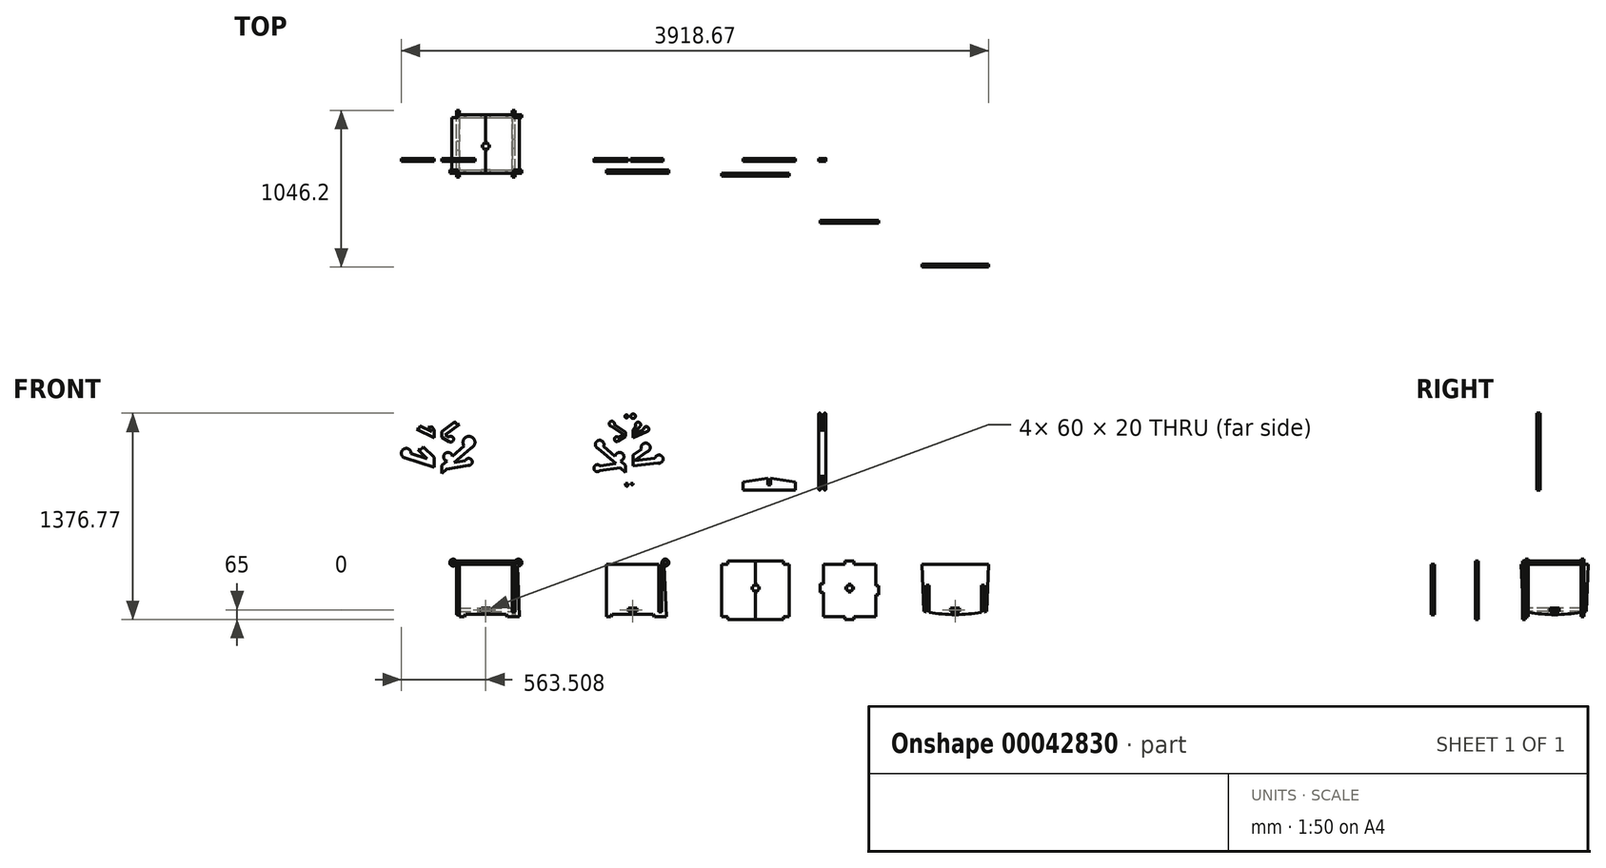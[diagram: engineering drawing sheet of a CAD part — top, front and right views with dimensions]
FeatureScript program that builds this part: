
annotation { "Feature Type Name" : "Feature", "Feature Type Description" : "" }
export const myFeature = defineFeature(function(context is Context, id is Id, definition is map)
    precondition{}
    {
        {
            var Q0;
            Q0=qCreatedBy(makeId("Top.planeOp"),FACE);
            var sketch = newSketch(context, id + "F0", { "sketchPlane" : qUnion([Q0])});
            skLineSegment(sketch, "E0.bottom", {"start": v(249.97, 292.99) * mm, "end": v(599.97, 292.99) * mm});
            skLineSegment(sketch, "E0.top", {"start": v(249.97, -57.01) * mm, "end": v(599.97, -57.01) * mm});
            skLineSegment(sketch, "E0.left", {"start": v(249.97, 292.99) * mm, "end": v(249.97, -57.01) * mm});
            skLineSegment(sketch, "E0.right", {"start": v(599.97, 292.99) * mm, "end": v(599.97, -57.01) * mm});
            skLineSegment(sketch, "E1.rect.bottom", {"start": v(454.97, -77.01) * mm, "end": v(394.97, -77.01) * mm});
            skLineSegment(sketch, "E1.rect.top", {"start": v(454.97, -37.01) * mm, "end": v(394.97, -37.01) * mm});
            skLineSegment(sketch, "E1.rect.left", {"start": v(454.97, -77.01) * mm, "end": v(454.97, -37.01) * mm});
            skLineSegment(sketch, "E1.rect.right", {"start": v(394.97, -77.01) * mm, "end": v(394.97, -37.01) * mm});
            skPoint(sketch, "E1.rect.middle", {"position": v(424.97, -57.01) * mm});
            skLineSegment(sketch, "E2.rect.bottom", {"start": v(269.97, 73.3) * mm, "end": v(229.97, 73.3) * mm});
            skLineSegment(sketch, "E2.rect.top", {"start": v(269.97, 133.3) * mm, "end": v(229.97, 133.3) * mm});
            skLineSegment(sketch, "E2.rect.left", {"start": v(269.97, 73.3) * mm, "end": v(269.97, 133.3) * mm});
            skLineSegment(sketch, "E2.rect.right", {"start": v(229.97, 73.3) * mm, "end": v(229.97, 133.3) * mm});
            skPoint(sketch, "E2.rect.middle", {"position": v(249.97, 103.3) * mm});
            skLineSegment(sketch, "E3.rect.bottom", {"start": v(454.97, 272.99) * mm, "end": v(394.97, 272.99) * mm});
            skLineSegment(sketch, "E3.rect.top", {"start": v(454.97, 312.99) * mm, "end": v(394.97, 312.99) * mm});
            skLineSegment(sketch, "E3.rect.left", {"start": v(454.97, 272.99) * mm, "end": v(454.97, 312.99) * mm});
            skLineSegment(sketch, "E3.rect.right", {"start": v(394.97, 272.99) * mm, "end": v(394.97, 312.99) * mm});
            skPoint(sketch, "E3.rect.middle", {"position": v(424.97, 292.99) * mm});
            skLineSegment(sketch, "E4.rect.bottom", {"start": v(619.97, 87.99) * mm, "end": v(579.97, 87.99) * mm});
            skLineSegment(sketch, "E4.rect.top", {"start": v(619.97, 147.99) * mm, "end": v(579.97, 147.99) * mm});
            skLineSegment(sketch, "E4.rect.left", {"start": v(619.97, 87.99) * mm, "end": v(619.97, 147.99) * mm});
            skLineSegment(sketch, "E4.rect.right", {"start": v(579.97, 87.99) * mm, "end": v(579.97, 147.99) * mm});
            skPoint(sketch, "E4.rect.middle", {"position": v(599.97, 117.99) * mm});
            skSolve(sketch);
        }
        {
            var Q0;
            Q0=makeQuery(id+"F0.imprint","IMPRINT",FACE,{"disambiguationData":[TD([[makeQuery(id+"F0.imprint","IMPRINT",EDGE,{"derivedFrom":sQuery(id+"F0.wireOp",EDGE,"E0.bottom")}),-1.0]])]});
            var Q1;
            {var subQ3=sQuery(id+"F0.wireOp",EDGE,"E2.rect.right");Q1=makeQuery(id+"F0.imprint","IMPRINT",FACE,{"disambiguationData":[TD([[makeQuery(id+"F0.imprint","IMPRINT",EDGE,{"derivedFrom":subQ3}),-1.0]])]});}
            var Q2;
            {var subQ3=sQuery(id+"F0.wireOp",EDGE,"E3.rect.top");Q2=makeQuery(id+"F0.imprint","IMPRINT",FACE,{"disambiguationData":[TD([[makeQuery(id+"F0.imprint","IMPRINT",EDGE,{"derivedFrom":subQ3}),1.0]])]});}
            var Q3;
            {var subQ0=sQuery(id+"F0.wireOp",EDGE,"E4.rect.left");Q3=makeQuery(id+"F0.imprint","IMPRINT",FACE,{"disambiguationData":[TD([[makeQuery(id+"F0.imprint","IMPRINT",EDGE,{"derivedFrom":subQ0}),1.0]])]});}
            var Q4;
            {var subQ3=sQuery(id+"F0.wireOp",EDGE,"E1.rect.bottom");Q4=makeQuery(id+"F0.imprint","IMPRINT",FACE,{"disambiguationData":[TD([[makeQuery(id+"F0.imprint","IMPRINT",EDGE,{"derivedFrom":subQ3}),-1.0]])]});}
            var Q5;
            {var subQ3=sQuery(id+"F0.wireOp",EDGE,"E1.rect.top");Q5=makeQuery(id+"F0.imprint","IMPRINT",FACE,{"disambiguationData":[TD([[makeQuery(id+"F0.imprint","IMPRINT",EDGE,{"derivedFrom":subQ3}),1.0]])]});}
            var Q6;
            {var subQ0=sQuery(id+"F0.wireOp",EDGE,"E4.rect.right");Q6=makeQuery(id+"F0.imprint","IMPRINT",FACE,{"disambiguationData":[TD([[makeQuery(id+"F0.imprint","IMPRINT",EDGE,{"derivedFrom":subQ0}),-1.0]])]});}
            var Q7;
            {var subQ3=sQuery(id+"F0.wireOp",EDGE,"E3.rect.bottom");Q7=makeQuery(id+"F0.imprint","IMPRINT",FACE,{"disambiguationData":[TD([[makeQuery(id+"F0.imprint","IMPRINT",EDGE,{"derivedFrom":subQ3}),-1.0]])]});}
            var Q8;
            {var subQ0=sQuery(id+"F0.wireOp",EDGE,"E2.rect.left");Q8=makeQuery(id+"F0.imprint","IMPRINT",FACE,{"disambiguationData":[TD([[makeQuery(id+"F0.imprint","IMPRINT",EDGE,{"derivedFrom":subQ0}),1.0]])]});}
            extrude(context, id + "F1", {"entities" : qUnion([Q0, Q1, Q2, Q3, Q4, Q5, Q6, Q7, Q8]), "depth" : 20 * mm});
        }
        {
            var Q0;
            {var subQ0=sQuery(id+"F0.wireOp",EDGE,"E0.top");Q0=makeQuery(id+"F1.opExtrude","SWEPT_FACE",FACE,{"disambiguationData":[OSD([subQ0]),TDD([makeQuery(id+"F0.imprint","IMPRINT",EDGE,{"disambiguationData":[TD([[makeQuery(id+"F0.imprint","INTERSECT",VERTEX,{"derivedFrom":[subQ0,sQuery(id+"F0.wireOp",EDGE,"E0.left")]}),-1.0]])],"derivedFrom":subQ0})])]});}
            var sketch = newSketch(context, id + "F2", { "sketchPlane" : qUnion([Q0])});
            skLineSegment(sketch, "E5.bottom", {"start": v(249.97, -35) * mm, "end": v(599.97, -35) * mm});
            skLineSegment(sketch, "E5.top", {"start": v(249.97, 315) * mm, "end": v(599.97, 315) * mm});
            skLineSegment(sketch, "E5.left", {"start": v(249.97, -35) * mm, "end": v(249.97, 315) * mm});
            skLineSegment(sketch, "E5.right", {"start": v(599.97, -35) * mm, "end": v(599.97, 315) * mm});
            skLineSegment(sketch, "E6.rect.top", {"start": v(619.97, 175) * mm, "end": v(599.97, 175) * mm});
            skPoint(sketch, "E6.rect.middle", {"position": v(599.97, 140) * mm});
            skLineSegment(sketch, "E7.rect.top", {"start": v(229.97, 175) * mm, "end": v(249.97, 175) * mm});
            skPoint(sketch, "E7.rect.middle", {"position": v(249.97, 140) * mm});
            skLineSegment(sketch, "E8", {"start": v(249.97, -60.28) * mm, "end": v(249.97, -93.17) * mm, "construction": true});
            skLineSegment(sketch, "E9", {"start": v(249.97, -76.72) * mm, "end": v(599.97, -76.72) * mm, "construction": true});
            skLineSegment(sketch, "E10", {"start": v(599.97, -60.28) * mm, "end": v(599.97, -93.17) * mm, "construction": true});
            skLineSegment(sketch, "E11", {"start": v(279.97, -60.28) * mm, "end": v(279.97, -93.17) * mm, "construction": true});
            skLineSegment(sketch, "E12", {"start": v(569.97, -60.28) * mm, "end": v(569.97, -93.17) * mm, "construction": true});
            skLineSegment(sketch, "E13", {"start": v(279.97, -35) * mm, "end": v(288.63, -20) * mm});
            skLineSegment(sketch, "E14", {"start": v(288.63, -20) * mm, "end": v(561.3, -20) * mm});
            skLineSegment(sketch, "E15", {"start": v(561.3, -20) * mm, "end": v(569.97, -35) * mm});
            skLineSegment(sketch, "E16", {"start": v(619.97, 175) * mm, "end": v(619.97, 315) * mm});
            skLineSegment(sketch, "E17", {"start": v(619.97, 315) * mm, "end": v(634.97, 315) * mm});
            skLineSegment(sketch, "E18", {"start": v(634.97, 315) * mm, "end": v(649.97, -35) * mm});
            skLineSegment(sketch, "E19", {"start": v(649.97, -35) * mm, "end": v(599.97, -35) * mm});
            skLineSegment(sketch, "E20", {"start": v(599.97, -76.72) * mm, "end": v(649.97, -76.72) * mm, "construction": true});
            skLineSegment(sketch, "E21", {"start": v(424.97, -76.72) * mm, "end": v(424.97, -147.18) * mm, "construction": true});
            skLineSegment(sketch, "E22.MirrorCS", {"start": v(199.97, -35) * mm, "end": v(249.97, -35) * mm});
            skLineSegment(sketch, "E23.MirrorCS", {"start": v(214.97, 315) * mm, "end": v(199.97, -35) * mm});
            skLineSegment(sketch, "E24.MirrorCS", {"start": v(229.97, 315) * mm, "end": v(214.97, 315) * mm});
            skLineSegment(sketch, "E25.MirrorCS", {"start": v(229.97, 175) * mm, "end": v(229.97, 315) * mm});
            skCircle(sketch, "E26", {"center": v(642.97, 324.97) * mm, "radius": 13 * mm});
            skCircle(sketch, "E27.0", {"center": v(642.97, 324.97) * mm, "radius": 23 * mm});
            skCircle(sketch, "E28.MirrorC", {"center": v(206.97, 324.97) * mm, "radius": 23 * mm});
            skCircle(sketch, "E29.MirrorC", {"center": v(206.97, 324.97) * mm, "radius": 13 * mm});
            skLineSegment(sketch, "E30.bottom", {"start": v(619.97, 315) * mm, "end": v(627.72, 315) * mm});
            skLineSegment(sketch, "E30.top", {"start": v(619.97, 324.97) * mm, "end": v(627.72, 324.97) * mm});
            skLineSegment(sketch, "E30.left", {"start": v(619.97, 315) * mm, "end": v(619.97, 324.97) * mm});
            skLineSegment(sketch, "E30.right", {"start": v(627.72, 315) * mm, "end": v(627.72, 324.97) * mm});
            skLineSegment(sketch, "E31.MirrorCS", {"start": v(229.97, 315) * mm, "end": v(229.97, 324.97) * mm});
            skSolve(sketch);
        }
        {
            var Q0;
            {var subQ0=sQuery(id+"F2.wireOp",EDGE,"E7.rect.left");Q0=makeQuery(id+"F2.imprint","IMPRINT",FACE,{"disambiguationData":[TD([[makeQuery(id+"F2.imprint","IMPRINT",EDGE,{"derivedFrom":subQ0}),-1.0]])]});}
            var Q1;
            {var subQ7=sQuery(id+"F2.wireOp",EDGE,"E5.top");Q1=makeQuery(id+"F2.imprint","IMPRINT",FACE,{"disambiguationData":[TD([[makeQuery(id+"F2.imprint","IMPRINT",EDGE,{"derivedFrom":subQ7}),-1.0]])]});}
            var Q2;
            {var subQ0=sQuery(id+"F2.wireOp",EDGE,"E6.rect.left");Q2=makeQuery(id+"F2.imprint","IMPRINT",FACE,{"disambiguationData":[TD([[makeQuery(id+"F2.imprint","IMPRINT",EDGE,{"derivedFrom":subQ0}),1.0]])]});}
            var Q3;
            {var subQ0=sQuery(id+"F2.wireOp",EDGE,"E6.rect.right");Q3=makeQuery(id+"F2.imprint","IMPRINT",FACE,{"disambiguationData":[TD([[makeQuery(id+"F2.imprint","IMPRINT",EDGE,{"derivedFrom":subQ0}),-1.0]])]});}
            var Q4;
            {var subQ3=sQuery(id+"F2.wireOp",EDGE,"E7.rect.right");Q4=makeQuery(id+"F2.imprint","IMPRINT",FACE,{"disambiguationData":[TD([[makeQuery(id+"F2.imprint","IMPRINT",EDGE,{"derivedFrom":subQ3}),1.0]])]});}
            var Q5;
            {var subQ0=sQuery(id+"F0.wireOp",EDGE,"E0.top");var subQ1=sQuery(id+"F0.wireOp",EDGE,"E1.rect.right");var subQ3=makeQuery(id+"F1.opExtrude","SWEPT_EDGE",EDGE,{"disambiguationData":[OSD([subQ0,subQ1])]});Q5=makeQuery(id+"F2.imprint","IMPRINT",FACE,{"disambiguationData":[TD([[makeQuery(id+"F2.imprint","IMPRINT",EDGE,{"derivedFrom":subQ3}),-1.0]])]});}
            var Q6;
            {var subQ2=sQuery(id+"F2.wireOp",EDGE,"E22.MirrorCS");Q6=makeQuery(id+"F2.imprint","IMPRINT",FACE,{"disambiguationData":[TD([[makeQuery(id+"F2.imprint","IMPRINT",EDGE,{"derivedFrom":subQ2}),1.0]])]});}
            var Q7;
            {var subQ1=sQuery(id+"F2.wireOp",EDGE,"E6.rect.top");Q7=makeQuery(id+"F2.imprint","IMPRINT",FACE,{"disambiguationData":[TD([[makeQuery(id+"F2.imprint","IMPRINT",EDGE,{"derivedFrom":subQ1}),1.0]])]});}
            var Q8;
            {var subQ3=sQuery(id+"F2.wireOp",EDGE,"E23.MirrorCS");var subQ5=sQuery(id+"F2.wireOp",EDGE,"E28.MirrorC");var subQ7=makeQuery(id+"F2.imprint","INTERSECT",VERTEX,{"derivedFrom":[subQ3,subQ5]});Q8=makeQuery(id+"F2.imprint","IMPRINT",FACE,{"disambiguationData":[TD([[makeQuery(id+"F2.imprint","IMPRINT",EDGE,{"disambiguationData":[TD([[subQ7,1.0]])],"derivedFrom":subQ3}),-1.0]])]});}
            var Q9;
            {var subQ3=sQuery(id+"F2.wireOp",EDGE,"E23.MirrorCS");var subQ5=sQuery(id+"F2.wireOp",EDGE,"E28.MirrorC");var subQ7=makeQuery(id+"F2.imprint","INTERSECT",VERTEX,{"derivedFrom":[subQ3,subQ5]});Q9=makeQuery(id+"F2.imprint","IMPRINT",FACE,{"disambiguationData":[TD([[makeQuery(id+"F2.imprint","IMPRINT",EDGE,{"disambiguationData":[TD([[subQ7,1.0]])],"derivedFrom":subQ3}),1.0]])]});}
            var Q10;
            {var subQ5=sQuery(id+"F2.wireOp",EDGE,"E27.0");var subQ7=sQuery(id+"F2.wireOp",EDGE,"E18");var subQ9=makeQuery(id+"F2.imprint","INTERSECT",VERTEX,{"derivedFrom":[subQ7,subQ5]});Q10=makeQuery(id+"F2.imprint","IMPRINT",FACE,{"disambiguationData":[TD([[makeQuery(id+"F2.imprint","IMPRINT",EDGE,{"disambiguationData":[TD([[subQ9,1.0]])],"derivedFrom":subQ7}),-1.0]])]});}
            var Q11;
            {var subQ0=sQuery(id+"F2.wireOp",EDGE,"E30.right");Q11=makeQuery(id+"F2.imprint","IMPRINT",FACE,{"disambiguationData":[TD([[makeQuery(id+"F2.imprint","IMPRINT",EDGE,{"derivedFrom":subQ0}),1.0]])]});}
            var Q12;
            {var subQ0=sQuery(id+"F2.wireOp",EDGE,"E30.right");Q12=makeQuery(id+"F2.imprint","IMPRINT",FACE,{"disambiguationData":[TD([[makeQuery(id+"F2.imprint","IMPRINT",EDGE,{"derivedFrom":subQ0}),-1.0]])]});}
            var Q13;
            {var subQ0=sQuery(id+"F2.wireOp",EDGE,"E30.left");Q13=makeQuery(id+"F2.imprint","IMPRINT",FACE,{"disambiguationData":[TD([[makeQuery(id+"F2.imprint","IMPRINT",EDGE,{"derivedFrom":subQ0}),-1.0]])]});}
            var Q14;
            {var subQ0=sQuery(id+"F2.wireOp",EDGE,"E31.MirrorCS");Q14=makeQuery(id+"F2.imprint","IMPRINT",FACE,{"disambiguationData":[TD([[makeQuery(id+"F2.imprint","IMPRINT",EDGE,{"derivedFrom":subQ0}),1.0]])]});}
            extrude(context, id + "F3", {"entities" : qUnion([Q0, Q1, Q2, Q3, Q4, Q5, Q6, Q7, Q8, Q9, Q10, Q11, Q12, Q13, Q14]), "depth" : 20 * mm});
        }
        {
            var Q0;
            Q0=makeQuery(id+"F3.opExtrude","CAP_FACE",FACE,{"disambiguationData":[OSD([sQuery(id+"F2.wireOp",EDGE,"E5.bottom"),sQuery(id+"F2.wireOp",EDGE,"E5.top"),sQuery(id+"F2.wireOp",EDGE,"E5.left"),sQuery(id+"F2.wireOp",EDGE,"E5.right"),sQuery(id+"F2.wireOp",EDGE,"E6.rect.bottom"),sQuery(id+"F2.wireOp",EDGE,"E6.rect.top"),sQuery(id+"F2.wireOp",EDGE,"E6.rect.left"),sQuery(id+"F2.wireOp",EDGE,"E7.rect.bottom"),sQuery(id+"F2.wireOp",EDGE,"E7.rect.top"),sQuery(id+"F2.wireOp",EDGE,"E7.rect.left")])],"isStart":true});
            cPlane(context, id + "F4", {"entities" : qUnion([Q0]), "cplaneType" : CPlaneType.OFFSET, "offset" : 175 * mm, "width" : 150 * mm, "height" : 150 * mm});
        }
        {
            var Q0;
            Q0=makeQuery(id+"F3.opExtrude","SWEPT_BODY",BODY,{"disambiguationData":[OSD([sQuery(id+"F2.wireOp",EDGE,"E5.bottom"),sQuery(id+"F2.wireOp",EDGE,"E5.top"),sQuery(id+"F2.wireOp",EDGE,"E5.left"),sQuery(id+"F2.wireOp",EDGE,"E5.right"),sQuery(id+"F2.wireOp",EDGE,"E6.rect.bottom"),sQuery(id+"F2.wireOp",EDGE,"E6.rect.top"),sQuery(id+"F2.wireOp",EDGE,"E6.rect.left"),sQuery(id+"F2.wireOp",EDGE,"E7.rect.bottom"),sQuery(id+"F2.wireOp",EDGE,"E7.rect.top"),sQuery(id+"F2.wireOp",EDGE,"E7.rect.left")])]});
            var Q1;
            Q1=qCreatedBy(id+"F4.planeOp",FACE);
            mirror(context, id + "F5", {"entities" : qUnion([Q0]), "mirrorPlane" : qUnion([Q1])});
        }
        {
            var Q0;
            {var subQ0=sQuery(id+"F2.wireOp",EDGE,"E5.right");Q0=makeQuery(id+"F3.opExtrude","SWEPT_FACE",FACE,{"disambiguationData":[OSD([subQ0]),TDD([makeQuery(id+"F2.imprint","IMPRINT",EDGE,{"disambiguationData":[TD([[makeQuery(id+"F2.imprint","INTERSECT",VERTEX,{"derivedFrom":[sQuery(id+"F2.wireOp",EDGE,"E5.top"),subQ0]}),1.0]])],"derivedFrom":subQ0})])]});}
            var sketch = newSketch(context, id + "F6", { "sketchPlane" : qUnion([Q0])});
            skLineSegment(sketch, "E32.bottom", {"start": v(-105.2, 315) * mm, "end": v(341.17, 315) * mm});
            skLineSegment(sketch, "E33", {"start": v(-105.2, 315) * mm, "end": v(-92.01, 0.28) * mm});
            skLineSegment(sketch, "E34", {"start": v(341.17, 315) * mm, "end": v(327.99, 0.28) * mm});
            skLineSegment(sketch, "E35", {"start": v(-97.01, -36.47) * mm, "end": v(-97.01, -59.46) * mm, "construction": true});
            skLineSegment(sketch, "E36", {"start": v(-97.01, -47.97) * mm, "end": v(332.99, -47.97) * mm, "construction": true});
            skLineSegment(sketch, "E37", {"start": v(332.99, -36.47) * mm, "end": v(332.99, -59.46) * mm, "construction": true});
            skLineSegment(sketch, "E38", {"start": v(-77.01, -36.47) * mm, "end": v(-77.01, -59.46) * mm, "construction": true});
            skLineSegment(sketch, "E39", {"start": v(312.99, -36.47) * mm, "end": v(312.99, -59.46) * mm, "construction": true});
            skArc(sketch, "E40", {"start": v(-92.01, 0.28) * mm, "mid": v(117.99, -22.2) * mm, "end": v(327.99, 0.28) * mm});
            skLineSegment(sketch, "E41", {"start": v(117.99, -99.63) * mm, "end": v(117.99, -121.43) * mm, "construction": true});
            skPoint(sketch, "E41.startSnap0", {"position": v(117.99, -22.2) * mm});
            skLineSegment(sketch, "E42", {"start": v(-92.01, -99.63) * mm, "end": v(-92.01, -121.43) * mm, "construction": true});
            skLineSegment(sketch, "E43", {"start": v(-92.01, -110.53) * mm, "end": v(117.99, -110.53) * mm, "construction": true});
            skLineSegment(sketch, "E44", {"start": v(327.99, -99.63) * mm, "end": v(327.99, -121.43) * mm, "construction": true});
            skLineSegment(sketch, "E45", {"start": v(117.99, -110.53) * mm, "end": v(327.99, -110.53) * mm, "construction": true});
            skPoint(sketch, "E46", {"position": v(117.99, 315) * mm});
            skPoint(sketch, "E47", {"position": v(117.99, -47.97) * mm});
            skSolve(sketch);
        }
        {
            var Q0;
            {var subQ0=sQuery(id+"F2.wireOp",EDGE,"E5.right");var subQ1=sQuery(id+"F2.wireOp",EDGE,"E6.rect.top");Q0=makeQuery(id+"F6.imprint","IMPRINT",FACE,{"disambiguationData":[TD([[makeQuery(id+"F6.imprint","IMPRINT",EDGE,{"derivedFrom":makeQuery(id+"F3.opExtrude","SWEPT_EDGE",EDGE,{"disambiguationData":[OSD([subQ0,subQ1])]})}),1.0]])]});}
            var Q1;
            {var subQ6=sQuery(id+"F6.wireOp",EDGE,"E33");Q1=makeQuery(id+"F6.imprint","IMPRINT",FACE,{"disambiguationData":[TD([[makeQuery(id+"F6.imprint","IMPRINT",EDGE,{"derivedFrom":subQ6}),1.0]])]});}
            extrude(context, id + "F7", {"entities" : qUnion([Q0, Q1]), "depth" : 20 * mm});
        }
        {
            var Q0;
            {var subQ0=sQuery(id+"F0.wireOp",EDGE,"E0.left");Q0=makeQuery(id+"F1.opExtrude","SWEPT_FACE",FACE,{"disambiguationData":[OSD([subQ0]),TDD([makeQuery(id+"F0.imprint","IMPRINT",EDGE,{"disambiguationData":[TD([[makeQuery(id+"F0.imprint","INTERSECT",VERTEX,{"derivedFrom":[sQuery(id+"F0.wireOp",EDGE,"E0.top"),subQ0]}),1.0]])],"derivedFrom":subQ0})])]});}
            cPlane(context, id + "F8", {"entities" : qUnion([Q0]), "cplaneType" : CPlaneType.OFFSET, "offset" : 175 * mm, "oppositeDirection" : true, "width" : 150 * mm, "height" : 150 * mm});
        }
        {
            var Q0;
            Q0=makeQuery(id+"F5.opPattern","COPY",FACE,{"derivedFrom":makeQuery(id+"F3.opExtrude","SWEPT_FACE",FACE,{"disambiguationData":[OSD([sQuery(id+"F2.wireOp",EDGE,"E5.top")])]}),"instanceName":"1"});
            var sketch = newSketch(context, id + "F9", { "sketchPlane" : qUnion([Q0])});
            skLineSegment(sketch, "E48.bottom", {"start": v(199.64, 292.99) * mm, "end": v(424.97, 292.99) * mm});
            skLineSegment(sketch, "E48.top", {"start": v(199.64, -57.01) * mm, "end": v(424.97, -57.01) * mm});
            skLineSegment(sketch, "E48.left", {"start": v(199.64, 292.99) * mm, "end": v(199.64, -57.01) * mm});
            skLineSegment(sketch, "E48.right", {"start": v(424.97, 292.99) * mm, "end": v(424.97, -57.01) * mm});
            skLineSegment(sketch, "E49.bottom", {"start": v(199.64, 292.99) * mm, "end": v(214.64, 292.99) * mm});
            skLineSegment(sketch, "E49.top", {"start": v(199.64, 312.99) * mm, "end": v(214.64, 312.99) * mm});
            skLineSegment(sketch, "E49.left", {"start": v(199.64, 292.99) * mm, "end": v(199.64, 312.99) * mm});
            skLineSegment(sketch, "E49.right", {"start": v(214.64, 292.99) * mm, "end": v(214.64, 312.99) * mm});
            skLineSegment(sketch, "E50.bottom", {"start": v(199.64, -57.01) * mm, "end": v(214.64, -57.01) * mm});
            skLineSegment(sketch, "E50.top", {"start": v(199.64, -72.01) * mm, "end": v(214.64, -72.01) * mm});
            skLineSegment(sketch, "E50.left", {"start": v(199.64, -57.01) * mm, "end": v(199.64, -72.01) * mm});
            skLineSegment(sketch, "E50.right", {"start": v(214.64, -57.01) * mm, "end": v(214.64, -72.01) * mm});
            skLineSegment(sketch, "E51.bottom", {"start": v(424.97, 292.99) * mm, "end": v(239.97, 292.99) * mm});
            skLineSegment(sketch, "E51.top", {"start": v(424.97, 312.99) * mm, "end": v(239.97, 312.99) * mm});
            skLineSegment(sketch, "E51.left", {"start": v(424.97, 292.99) * mm, "end": v(424.97, 312.99) * mm});
            skLineSegment(sketch, "E51.right", {"start": v(239.97, 292.99) * mm, "end": v(239.97, 312.99) * mm});
            skLineSegment(sketch, "E52", {"start": v(176.2, 117.99) * mm, "end": v(109.97, 117.99) * mm, "construction": true});
            skPoint(sketch, "E52.startSnap0", {"position": v(199.64, 117.99) * mm});
            skLineSegment(sketch, "E53.MirrorCS", {"start": v(424.97, -77.01) * mm, "end": v(239.97, -77.01) * mm});
            skLineSegment(sketch, "E54.MirrorCS", {"start": v(239.97, -57.01) * mm, "end": v(239.97, -77.01) * mm});
            skLineSegment(sketch, "E55.MirrorCS", {"start": v(424.97, -57.01) * mm, "end": v(424.97, -77.01) * mm});
            skSolve(sketch);
        }
        {
            var Q0;
            Q0=makeQuery(id+"F9.imprint","IMPRINT",FACE,{"disambiguationData":[TD([[makeQuery(id+"F9.imprint","IMPRINT",EDGE,{"derivedFrom":sQuery(id+"F9.wireOp",EDGE,"E48.top")}),1.0]])]});
            var Q1;
            Q1=makeQuery(id+"F9.imprint","IMPRINT",FACE,{"disambiguationData":[TD([[makeQuery(id+"F9.imprint","IMPRINT",EDGE,{"derivedFrom":sQuery(id+"F9.wireOp",EDGE,"E49.bottom")}),1.0]])]});
            var Q2;
            Q2=makeQuery(id+"F9.imprint","IMPRINT",FACE,{"disambiguationData":[TD([[makeQuery(id+"F9.imprint","IMPRINT",EDGE,{"derivedFrom":sQuery(id+"F9.wireOp",EDGE,"E50.bottom")}),-1.0]])]});
            var Q3;
            {var subQ3=sQuery(id+"F9.wireOp",EDGE,"E51.left");Q3=makeQuery(id+"F9.imprint","IMPRINT",FACE,{"disambiguationData":[TD([[makeQuery(id+"F9.imprint","IMPRINT",EDGE,{"derivedFrom":subQ3}),1.0]])]});}
            var Q4;
            Q4=makeQuery(id+"F9.imprint","IMPRINT",FACE,{"disambiguationData":[TD([[makeQuery(id+"F9.imprint","IMPRINT",EDGE,{"derivedFrom":sQuery(id+"F9.wireOp",EDGE,"E53.MirrorCS")}),-1.0]])]});
            var Q5;
            {var subQ2=sQuery(id+"F9.wireOp",EDGE,"E51.right");Q5=makeQuery(id+"F9.imprint","IMPRINT",FACE,{"disambiguationData":[TD([[makeQuery(id+"F9.imprint","IMPRINT",EDGE,{"derivedFrom":subQ2}),-1.0]])]});}
            extrude(context, id + "F10", {"entities" : qUnion([Q0, Q1, Q2, Q3, Q4, Q5]), "depth" : 20 * mm});
        }
        {
            var Q0;
            Q0=makeQuery(id+"F10.opExtrude","SWEPT_BODY",BODY,{"disambiguationData":[OSD([sQuery(id+"F9.wireOp",EDGE,"E48.bottom"),sQuery(id+"F9.wireOp",EDGE,"E48.top"),sQuery(id+"F9.wireOp",EDGE,"E48.left"),sQuery(id+"F9.wireOp",EDGE,"E48.right"),sQuery(id+"F9.wireOp",EDGE,"E49.top"),sQuery(id+"F9.wireOp",EDGE,"E49.left"),sQuery(id+"F9.wireOp",EDGE,"E49.right"),sQuery(id+"F9.wireOp",EDGE,"E50.top"),sQuery(id+"F9.wireOp",EDGE,"E50.left"),sQuery(id+"F9.wireOp",EDGE,"E50.right")])]});
            var Q1;
            Q1=qCreatedBy(id+"F8.planeOp",FACE);
            mirror(context, id + "F11", {"entities" : qUnion([Q0]), "mirrorPlane" : qUnion([Q1])});
        }
        {
            var Q0;
            Q0=makeQuery(id+"F7.opExtrude","CAP_FACE",FACE,{"disambiguationData":[OSD([sQuery(id+"F6.wireOp",EDGE,"E32.bottom"),sQuery(id+"F6.wireOp",EDGE,"E33"),sQuery(id+"F6.wireOp",EDGE,"E34"),sQuery(id+"F6.wireOp",EDGE,"E40")])],"isStart":false});
            var sketch = newSketch(context, id + "F12", { "sketchPlane" : qUnion([Q0])});
            skLineSegment(sketch, "E56.bottom", {"start": v(-77.01, 175) * mm, "end": v(-57.01, 175) * mm});
            skLineSegment(sketch, "E56.top", {"start": v(-77.01, -14.46) * mm, "end": v(-57.01, -14.46) * mm});
            skLineSegment(sketch, "E56.left", {"start": v(-77.01, 175) * mm, "end": v(-77.01, -14.46) * mm});
            skLineSegment(sketch, "E56.right", {"start": v(-57.01, 175) * mm, "end": v(-57.01, -14.46) * mm});
            skLineSegment(sketch, "E57", {"start": v(117.99, -31.68) * mm, "end": v(117.99, -70.5) * mm, "construction": true});
            skPoint(sketch, "E57.startSnap0", {"position": v(117.99, -22.2) * mm});
            skLineSegment(sketch, "E58.MirrorCS", {"start": v(292.99, 175) * mm, "end": v(292.99, -14.46) * mm});
            skLineSegment(sketch, "E59.MirrorCS", {"start": v(312.99, 175) * mm, "end": v(292.99, 175) * mm});
            skLineSegment(sketch, "E60.MirrorCS", {"start": v(312.99, 175) * mm, "end": v(312.99, -14.46) * mm});
            skLineSegment(sketch, "E61.MirrorCS", {"start": v(312.99, -14.46) * mm, "end": v(292.99, -14.46) * mm});
            skSolve(sketch);
        }
        {
            var Q0;
            {var subQ0=sQuery(id+"F12.wireOp",EDGE,"E56.bottom");Q0=makeQuery(id+"F12.imprint","IMPRINT",FACE,{"disambiguationData":[TD([[makeQuery(id+"F12.imprint","IMPRINT",EDGE,{"derivedFrom":subQ0}),-1.0]])]});}
            var Q1;
            {var subQ0=sQuery(id+"F12.wireOp",EDGE,"E59.MirrorCS");Q1=makeQuery(id+"F12.imprint","IMPRINT",FACE,{"disambiguationData":[TD([[makeQuery(id+"F12.imprint","IMPRINT",EDGE,{"derivedFrom":subQ0}),1.0]])]});}
            var Q2;
            Q2=makeQuery(id+"F7.opExtrude","CAP_FACE",FACE,{"disambiguationData":[OSD([sQuery(id+"F6.wireOp",EDGE,"E32.bottom"),sQuery(id+"F6.wireOp",EDGE,"E33"),sQuery(id+"F6.wireOp",EDGE,"E34"),sQuery(id+"F6.wireOp",EDGE,"E40")])],"isStart":true});
            extrude(context, id + "F13", {"entities" : qUnion([Q0, Q1]), "operationType" : NewBodyOperationType.REMOVE, "endBound" : BoundingType.UP_TO_SURFACE, "oppositeDirection" : true, "endBoundEntityFace" : qUnion([Q2]), "depth" : 25 * mm});
        }
        {
            var Q0;
            Q0=makeQuery(id+"F7.opExtrude","SWEPT_BODY",BODY,{"disambiguationData":[OSD([sQuery(id+"F6.wireOp",EDGE,"E32.bottom"),sQuery(id+"F6.wireOp",EDGE,"E32.top"),sQuery(id+"F6.wireOp",EDGE,"E33"),sQuery(id+"F6.wireOp",EDGE,"E34")])]});
            var Q1;
            Q1=qCreatedBy(id+"F8.planeOp",FACE);
            mirror(context, id + "F14", {"entities" : qUnion([Q0]), "mirrorPlane" : qUnion([Q1])});
        }
        {
            var Q0;
            Q0=makeQuery(id+"F1.opExtrude","SWEPT_BODY",BODY,{"disambiguationData":[OSD([sQuery(id+"F0.wireOp",EDGE,"E0.bottom"),sQuery(id+"F0.wireOp",EDGE,"E0.top"),sQuery(id+"F0.wireOp",EDGE,"E0.left"),sQuery(id+"F0.wireOp",EDGE,"E0.right"),sQuery(id+"F0.wireOp",EDGE,"E1.rect.bottom"),sQuery(id+"F0.wireOp",EDGE,"E1.rect.left"),sQuery(id+"F0.wireOp",EDGE,"E1.rect.right"),sQuery(id+"F0.wireOp",EDGE,"E2.rect.bottom"),sQuery(id+"F0.wireOp",EDGE,"E2.rect.top"),sQuery(id+"F0.wireOp",EDGE,"E2.rect.right"),sQuery(id+"F0.wireOp",EDGE,"E3.rect.top"),sQuery(id+"F0.wireOp",EDGE,"E3.rect.left"),sQuery(id+"F0.wireOp",EDGE,"E3.rect.right"),sQuery(id+"F0.wireOp",EDGE,"E4.rect.bottom"),sQuery(id+"F0.wireOp",EDGE,"E4.rect.top"),sQuery(id+"F0.wireOp",EDGE,"E4.rect.left")])]});
            var Q1;
            Q1=makeQuery(id+"F14.opPattern","COPY",BODY,{"derivedFrom":makeQuery(id+"F7.opExtrude","SWEPT_BODY",BODY,{"disambiguationData":[OSD([sQuery(id+"F6.wireOp",EDGE,"E32.bottom"),sQuery(id+"F6.wireOp",EDGE,"E33"),sQuery(id+"F6.wireOp",EDGE,"E34"),sQuery(id+"F6.wireOp",EDGE,"E40")])]}),"instanceName":"1"});
            var Q2;
            Q2=makeQuery(id+"F3.opExtrude","SWEPT_BODY",BODY,{"disambiguationData":[OSD([sQuery(id+"F2.wireOp",EDGE,"E5.bottom"),sQuery(id+"F2.wireOp",EDGE,"E5.top"),sQuery(id+"F2.wireOp",EDGE,"E5.left"),sQuery(id+"F2.wireOp",EDGE,"E5.right"),sQuery(id+"F2.wireOp",EDGE,"E6.rect.top"),sQuery(id+"F2.wireOp",EDGE,"E13"),sQuery(id+"F2.wireOp",EDGE,"E14"),sQuery(id+"F2.wireOp",EDGE,"E15"),sQuery(id+"F2.wireOp",EDGE,"E16"),sQuery(id+"F2.wireOp",EDGE,"E18"),sQuery(id+"F2.wireOp",EDGE,"E19"),sQuery(id+"F2.wireOp",EDGE,"E22.MirrorCS"),sQuery(id+"F2.wireOp",EDGE,"E23.MirrorCS"),sQuery(id+"F2.wireOp",EDGE,"E25.MirrorCS"),sQuery(id+"F2.wireOp",EDGE,"E7.rect.top"),sQuery(id+"F2.wireOp",EDGE,"E26"),sQuery(id+"F2.wireOp",EDGE,"E27.0"),sQuery(id+"F2.wireOp",EDGE,"E28.MirrorC"),sQuery(id+"F2.wireOp",EDGE,"E29.MirrorC"),sQuery(id+"F2.wireOp",EDGE,"E30.left"),sQuery(id+"F2.wireOp",EDGE,"E31.MirrorCS")])]});
            var Q3;
            Q3=makeQuery(id+"F7.opExtrude","SWEPT_BODY",BODY,{"disambiguationData":[OSD([sQuery(id+"F6.wireOp",EDGE,"E32.bottom"),sQuery(id+"F6.wireOp",EDGE,"E33"),sQuery(id+"F6.wireOp",EDGE,"E34"),sQuery(id+"F6.wireOp",EDGE,"E40")])]});
            var Q4;
            Q4=makeQuery(id+"F5.opPattern","COPY",BODY,{"derivedFrom":makeQuery(id+"F3.opExtrude","SWEPT_BODY",BODY,{"disambiguationData":[OSD([sQuery(id+"F2.wireOp",EDGE,"E5.bottom"),sQuery(id+"F2.wireOp",EDGE,"E5.top"),sQuery(id+"F2.wireOp",EDGE,"E5.left"),sQuery(id+"F2.wireOp",EDGE,"E5.right"),sQuery(id+"F2.wireOp",EDGE,"E6.rect.top"),sQuery(id+"F2.wireOp",EDGE,"E13"),sQuery(id+"F2.wireOp",EDGE,"E14"),sQuery(id+"F2.wireOp",EDGE,"E15"),sQuery(id+"F2.wireOp",EDGE,"E16"),sQuery(id+"F2.wireOp",EDGE,"E18"),sQuery(id+"F2.wireOp",EDGE,"E19"),sQuery(id+"F2.wireOp",EDGE,"E22.MirrorCS"),sQuery(id+"F2.wireOp",EDGE,"E23.MirrorCS"),sQuery(id+"F2.wireOp",EDGE,"E25.MirrorCS"),sQuery(id+"F2.wireOp",EDGE,"E7.rect.top"),sQuery(id+"F2.wireOp",EDGE,"E26"),sQuery(id+"F2.wireOp",EDGE,"E27.0"),sQuery(id+"F2.wireOp",EDGE,"E28.MirrorC"),sQuery(id+"F2.wireOp",EDGE,"E29.MirrorC"),sQuery(id+"F2.wireOp",EDGE,"E30.left"),sQuery(id+"F2.wireOp",EDGE,"E31.MirrorCS")])]}),"instanceName":"1"});
            booleanBodies(context, id + "F15", {"operationType" : BooleanOperationType.SUBTRACTION, "tools" : qUnion([Q0]), "targets" : qUnion([Q1, Q2, Q3, Q4]), "keepTools" : true});
        }
        {
            var Q0;
            Q0=qCreatedBy(makeId("Front.planeOp"),FACE);
            var sketch = newSketch(context, id + "F16", { "sketchPlane" : qUnion([Q0])});
            skLineSegment(sketch, "E62.rect.bottom", {"start": v(1718, 828.78) * mm, "end": v(1168, 828.78) * mm});
            skLineSegment(sketch, "E62.rect.top", {"start": v(1718, 1378.78) * mm, "end": v(1168, 1378.78) * mm});
            skLineSegment(sketch, "E62.rect.left", {"start": v(1718, 828.78) * mm, "end": v(1718, 1378.78) * mm});
            skLineSegment(sketch, "E62.rect.right", {"start": v(1168, 828.78) * mm, "end": v(1168, 1378.78) * mm});
            skPoint(sketch, "E62.rect.middle", {"position": v(1443, 1103.78) * mm});
            skLineSegment(sketch, "E63.rect.bottom", {"start": v(708.77, -109.93) * mm, "end": v(158.77, -109.93) * mm});
            skLineSegment(sketch, "E63.rect.top", {"start": v(708.77, 440.07) * mm, "end": v(158.77, 440.07) * mm});
            skLineSegment(sketch, "E63.rect.left", {"start": v(708.77, -109.93) * mm, "end": v(708.77, 440.07) * mm});
            skLineSegment(sketch, "E63.rect.right", {"start": v(158.77, -109.93) * mm, "end": v(158.77, 440.07) * mm});
            skPoint(sketch, "E63.rect.middle", {"position": v(433.77, 165.07) * mm});
            skSolve(sketch);
        }
        {
            var Q0;
            Q0=qCreatedBy(makeId("Front.planeOp"),FACE);
            var sketch = newSketch(context, id + "F17", { "sketchPlane" : qUnion([Q0])});
            skLineSegment(sketch, "E64.bottom", {"start": v(1358, 1302) * mm, "end": v(1408, 1302) * mm, "construction": true});
            skLineSegment(sketch, "E64.top", {"start": v(1358, 852) * mm, "end": v(1408, 852) * mm});
            skLineSegment(sketch, "E64.left", {"start": v(1358, 1302) * mm, "end": v(1358, 852) * mm});
            skLineSegment(sketch, "E64.right", {"start": v(1408, 1302) * mm, "end": v(1408, 852) * mm});
            skLineSegment(sketch, "E65", {"start": v(1408, 1182.06) * mm, "end": v(1452.39, 1231.49) * mm});
            skLineSegment(sketch, "E66.0", {"start": v(1400.17, 1203.27) * mm, "end": v(1429.7, 1236.16) * mm});
            skLineSegment(sketch, "E67.0", {"start": v(1397.46, 1175.45) * mm, "end": v(1492.52, 1216.86) * mm});
            skLineSegment(sketch, "E68", {"start": v(1358, 927.33) * mm, "end": v(1173.73, 1087.78) * mm});
            skLineSegment(sketch, "E69", {"start": v(1408, 999.81) * mm, "end": v(1512.28, 1074.23) * mm});
            skLineSegment(sketch, "E70.0", {"start": v(1373.27, 960.45) * mm, "end": v(1192.82, 1117.57) * mm});
            skLineSegment(sketch, "E71.0", {"start": v(1378.97, 1022.1) * mm, "end": v(1467.65, 1085.37) * mm});
            skLineSegment(sketch, "E72", {"start": v(1383, 852) * mm, "end": v(1383, 933.07) * mm, "construction": true});
            skLineSegment(sketch, "E73", {"start": v(1373, 852) * mm, "end": v(1373, 957) * mm});
            skLineSegment(sketch, "E74", {"start": v(1373, 957) * mm, "end": v(1383, 957) * mm});
            skLineSegment(sketch, "E75.MirrorCS", {"start": v(1393, 957) * mm, "end": v(1383, 957) * mm});
            skLineSegment(sketch, "E76.MirrorCS", {"start": v(1393, 852) * mm, "end": v(1393, 957) * mm});
            skLineSegment(sketch, "E77", {"start": v(1373, 1302) * mm, "end": v(1373, 1197) * mm});
            skLineSegment(sketch, "E78", {"start": v(1373, 1197) * mm, "end": v(1383, 1197) * mm});
            skLineSegment(sketch, "E79.MirrorCS", {"start": v(1393, 1197) * mm, "end": v(1383, 1197) * mm});
            skLineSegment(sketch, "E80.MirrorCS", {"start": v(1393, 1302) * mm, "end": v(1393, 1197) * mm});
            skLineSegment(sketch, "E81.0", {"start": v(1396.4, 1153.18) * mm, "end": v(1499.96, 1198.29) * mm});
            skLineSegment(sketch, "E82", {"start": v(1383, 1197) * mm, "end": v(1383, 1316.53) * mm, "construction": true});
            skLineSegment(sketch, "E83.MirrorCS", {"start": v(1344.33, 1181.42) * mm, "end": v(1309.53, 1160.36) * mm});
            skLineSegment(sketch, "E84.MirrorCS", {"start": v(1362.91, 1169.3) * mm, "end": v(1307, 1135.45) * mm});
            skLineSegment(sketch, "E85.0", {"start": v(1358, 1196.33) * mm, "end": v(1265.39, 1258.24) * mm});
            skLineSegment(sketch, "E86", {"start": v(1393, 1302) * mm, "end": v(1393, 1312) * mm});
            skLineSegment(sketch, "E87", {"start": v(1393, 1312) * mm, "end": v(1408, 1312) * mm, "construction": true});
            skLineSegment(sketch, "E88", {"start": v(1408, 1312) * mm, "end": v(1408, 1302) * mm});
            skLineSegment(sketch, "E89.trimOffspring", {"start": v(1344.33, 1181.42) * mm, "end": v(1257.65, 1239.36) * mm});
            skArc(sketch, "E90", {"start": v(1309.53, 1160.36) * mm, "mid": v(1282.51, 1150.52) * mm, "end": v(1307, 1135.45) * mm});
            skCircle(sketch, "E91", {"center": v(1265.39, 1251.01) * mm, "radius": 17.5 * mm});
            skCircle(sketch, "E92", {"center": v(1441.18, 1244.17) * mm, "radius": 17.5 * mm});
            skCircle(sketch, "E93", {"center": v(1495.32, 1215.12) * mm, "radius": 17.5 * mm});
            skCircle(sketch, "E94", {"center": v(1491.66, 1092.44) * mm, "radius": 30 * mm});
            skLineSegment(sketch, "E95", {"start": v(1336.86, 961.4) * mm, "end": v(1174.12, 936.9) * mm});
            skLineSegment(sketch, "E96.0", {"start": v(1326.54, 990.19) * mm, "end": v(1160.1, 965.12) * mm});
            skCircle(sketch, "E97", {"center": v(1169.54, 955.2) * mm, "radius": 23.45 * mm});
            skLineSegment(sketch, "E98", {"start": v(1398.44, 968.86) * mm, "end": v(1579.96, 990.46) * mm});
            skLineSegment(sketch, "E99.0", {"start": v(1409.02, 1005.36) * mm, "end": v(1580.25, 1025.75) * mm});
            skCircle(sketch, "E100", {"center": v(1580.25, 1015.46) * mm, "radius": 27.5 * mm});
            skCircle(sketch, "E101", {"center": v(1317.13, 1031.41) * mm, "radius": 29.16 * mm});
            skArc(sketch, "E102", {"start": v(1393, 852) * mm, "mid": v(1400.5, 844.5) * mm, "end": v(1408, 852) * mm});
            skLineSegment(sketch, "E103", {"start": v(1373, 852) * mm, "end": v(1373, 842.14) * mm});
            skLineSegment(sketch, "E104", {"start": v(1373, 842.14) * mm, "end": v(1358, 842.14) * mm, "construction": true});
            skLineSegment(sketch, "E105", {"start": v(1358, 842.14) * mm, "end": v(1358, 852) * mm});
            skArc(sketch, "E106", {"start": v(1358, 842.14) * mm, "mid": v(1365.5, 834.64) * mm, "end": v(1373, 842.14) * mm});
            skCircle(sketch, "E107", {"center": v(1408, 1302) * mm, "radius": 15.5 * mm});
            skCircle(sketch, "E108", {"center": v(1362.86, 1301.19) * mm, "radius": 10.16 * mm});
            skLineSegment(sketch, "E109", {"start": v(1991.8, 852) * mm, "end": v(1991.8, 1433.17) * mm, "construction": true});
            skLineSegment(sketch, "E110.MirrorCS", {"start": v(2679.56, 1314.27) * mm, "end": v(2679.56, 1209.27) * mm});
            skLineSegment(sketch, "E111.MirrorCS", {"start": v(2659.56, 1314.27) * mm, "end": v(2659.56, 1209.27) * mm});
            skLineSegment(sketch, "E112.MirrorCS", {"start": v(2679.56, 1209.27) * mm, "end": v(2669.56, 1209.27) * mm});
            skLineSegment(sketch, "E113.MirrorCS", {"start": v(2694.56, 1314.27) * mm, "end": v(2694.56, 816.77) * mm});
            skArc(sketch, "E114", {"start": v(2659.56, 1314.27) * mm, "mid": v(2652.06, 1321.77) * mm, "end": v(2644.56, 1314.27) * mm});
            skArc(sketch, "E115", {"start": v(2694.56, 1314.27) * mm, "mid": v(2687.06, 1321.77) * mm, "end": v(2679.56, 1314.27) * mm});
            skArc(sketch, "E116", {"start": v(2679.56, 816.77) * mm, "mid": v(2687.06, 809.27) * mm, "end": v(2694.56, 816.77) * mm});
            skLineSegment(sketch, "E117", {"start": v(2644.56, 1314.27) * mm, "end": v(2644.56, 816.77) * mm});
            skArc(sketch, "E118", {"start": v(2644.56, 816.77) * mm, "mid": v(2652.06, 809.27) * mm, "end": v(2659.56, 816.77) * mm});
            skLineSegment(sketch, "E119", {"start": v(2490.83, 809.27) * mm, "end": v(2140.83, 809.27) * mm});
            skPoint(sketch, "E119.startSnap0", {"position": v(2652.06, 809.27) * mm});
            skLineSegment(sketch, "E120", {"start": v(2140.83, 809.27) * mm, "end": v(2140.83, 864.27) * mm});
            skLineSegment(sketch, "E121", {"start": v(2140.83, 864.27) * mm, "end": v(2305.83, 889.27) * mm});
            skLineSegment(sketch, "E122", {"start": v(2305.83, 889.27) * mm, "end": v(2305.83, 844.27) * mm});
            skLineSegment(sketch, "E123", {"start": v(2305.83, 844.27) * mm, "end": v(2315.83, 844.27) * mm});
            skPoint(sketch, "E123.endSnap0", {"position": v(2315.83, 809.27) * mm});
            skLineSegment(sketch, "E124", {"start": v(2315.83, 778.06) * mm, "end": v(2315.83, 726.38) * mm, "construction": true});
            skLineSegment(sketch, "E125.MirrorCS", {"start": v(2325.83, 844.27) * mm, "end": v(2315.83, 844.27) * mm});
            skLineSegment(sketch, "E126.MirrorCS", {"start": v(2325.83, 889.27) * mm, "end": v(2325.83, 844.27) * mm});
            skLineSegment(sketch, "E127.MirrorCS", {"start": v(2490.83, 864.27) * mm, "end": v(2325.83, 889.27) * mm});
            skLineSegment(sketch, "E128.MirrorCS", {"start": v(2490.83, 809.27) * mm, "end": v(2490.83, 864.27) * mm});
            skLineSegment(sketch, "E129", {"start": v(2659.56, 1209.27) * mm, "end": v(2669.56, 1209.27) * mm});
            skLineSegment(sketch, "E130", {"start": v(2659.56, 901.77) * mm, "end": v(2679.56, 901.77) * mm});
            skLineSegment(sketch, "E131", {"start": v(2659.56, 901.77) * mm, "end": v(2659.56, 816.77) * mm});
            skLineSegment(sketch, "E132", {"start": v(2679.56, 901.77) * mm, "end": v(2679.56, 816.77) * mm});
            skLineSegment(sketch, "E133", {"start": v(744.9, 864.27) * mm, "end": v(744.9, 1433.17) * mm, "construction": true});
            skCircle(sketch, "E134.MirrorC", {"center": v(311.46, 996.99) * mm, "radius": 23.45 * mm});
            skLineSegment(sketch, "E135.MirrorCS", {"start": v(151.95, 947.01) * mm, "end": v(309.05, 974.06) * mm});
            skLineSegment(sketch, "E136.MirrorCS", {"start": v(160.68, 984.03) * mm, "end": v(322.24, 1011.85) * mm});
            skLineSegment(sketch, "E137.MirrorCS", {"start": v(116.52, 960.45) * mm, "end": v(296.96, 1117.57) * mm});
            skCircle(sketch, "E138.MirrorC", {"center": v(172.65, 1031.41) * mm, "radius": 29.16 * mm});
            skLineSegment(sketch, "E139.MirrorCS", {"start": v(131.77, 1302) * mm, "end": v(131.77, 852) * mm});
            skLineSegment(sketch, "E140.MirrorCS", {"start": v(116.77, 852) * mm, "end": v(116.77, 957) * mm});
            skLineSegment(sketch, "E141.MirrorCS", {"start": v(124.28, 1165.01) * mm, "end": v(180.19, 1131.18) * mm});
            skArc(sketch, "E142.MirrorCS", {"start": v(175.5, 1162.52) * mm, "mid": v(209.78, 1149.97) * mm, "end": v(177.59, 1132.75) * mm});
            skLineSegment(sketch, "E143.MirrorCS", {"start": v(145.46, 1181.42) * mm, "end": v(180.25, 1160.36) * mm});
            skLineSegment(sketch, "E144.MirrorCS", {"start": v(149.75, 1174.82) * mm, "end": v(249.05, 1248.08) * mm});
            skCircle(sketch, "E145.MirrorC", {"center": v(241.4, 1266.57) * mm, "radius": 20 * mm});
            skLineSegment(sketch, "E146.MirrorCS", {"start": v(128.5, 1196.43) * mm, "end": v(239.96, 1278.66) * mm});
            skCircle(sketch, "E147.MirrorC", {"center": v(126.93, 1301.19) * mm, "radius": 10.16 * mm});
            skLineSegment(sketch, "E148.MirrorCS", {"start": v(116.77, 1302) * mm, "end": v(116.77, 1197) * mm});
            skLineSegment(sketch, "E149.MirrorCS", {"start": v(96.77, 1302) * mm, "end": v(96.77, 1197) * mm});
            skCircle(sketch, "E150.MirrorC", {"center": v(81.77, 1302) * mm, "radius": 15.5 * mm});
            skLineSegment(sketch, "E151.MirrorCS", {"start": v(81.77, 1302) * mm, "end": v(81.77, 852) * mm});
            skLineSegment(sketch, "E152.MirrorCS", {"start": v(89.6, 1203.27) * mm, "end": v(60.08, 1236.16) * mm});
            skLineSegment(sketch, "E153.MirrorCS", {"start": v(83.21, 1179.68) * mm, "end": v(37.4, 1231.49) * mm});
            skCircle(sketch, "E154.MirrorC", {"center": v(48.6, 1244.17) * mm, "radius": 17.5 * mm});
            skLineSegment(sketch, "E155.MirrorCS", {"start": v(96.45, 1184.89) * mm, "end": v(-23.18, 1241.2) * mm});
            skLineSegment(sketch, "E156.MirrorCS", {"start": v(93.37, 1153.18) * mm, "end": v(-41.9, 1216.86) * mm});
            skCircle(sketch, "E157.MirrorC", {"center": v(-37.04, 1236.91) * mm, "radius": 22.5 * mm});
            skCircle(sketch, "E158.MirrorC", {"center": v(-22.28, 1110.43) * mm, "radius": 32.5 * mm});
            skLineSegment(sketch, "E159.MirrorCS", {"start": v(100.27, 1011.04) * mm, "end": v(-0.4, 1107.06) * mm});
            skLineSegment(sketch, "E160.MirrorCS", {"start": v(55.86, 998.12) * mm, "end": v(-47.47, 1096.67) * mm});
            skLineSegment(sketch, "E161.MirrorCS", {"start": v(91.75, 1000.91) * mm, "end": v(-123.18, 1067.74) * mm});
            skLineSegment(sketch, "E162.MirrorCS", {"start": v(88.96, 959.9) * mm, "end": v(-115.99, 1023.62) * mm});
            skCircle(sketch, "E163.MirrorC", {"center": v(-106.04, 1054.56) * mm, "radius": 32.5 * mm});
            skArc(sketch, "E164.MirrorCS", {"start": v(96.77, 852) * mm, "mid": v(89.27, 844.5) * mm, "end": v(81.77, 852) * mm});
            skLineSegment(sketch, "E165", {"start": v(96.77, 1197) * mm, "end": v(116.77, 1197) * mm});
            skLineSegment(sketch, "E166", {"start": v(96.77, 852) * mm, "end": v(96.77, 957) * mm});
            skArc(sketch, "E167", {"start": v(116.77, 852) * mm, "mid": v(124.27, 844.5) * mm, "end": v(131.77, 852) * mm});
            skLineSegment(sketch, "E168", {"start": v(96.77, 957) * mm, "end": v(116.77, 957) * mm});
            skCircle(sketch, "E169", {"center": v(312.6, 1127.28) * mm, "radius": 40 * mm});
            skLineSegment(sketch, "E170", {"start": v(124.11, 914.03) * mm, "end": v(341.7, 1103.49) * mm});
            skCircle(sketch, "E171", {"center": v(1184.77, 1112.62) * mm, "radius": 28.66 * mm});
            skSolve(sketch);
        }
        {
            var Q0;
            {var subQ1=sQuery(id+"F17.wireOp",EDGE,"E73");Q0=makeQuery(id+"F17.imprint","IMPRINT",FACE,{"disambiguationData":[TD([[makeQuery(id+"F17.imprint","IMPRINT",EDGE,{"derivedFrom":subQ1}),1.0]])]});}
            var Q1;
            {var subQ0=sQuery(id+"F17.wireOp",EDGE,"E83.MirrorCS");Q1=makeQuery(id+"F17.imprint","IMPRINT",FACE,{"disambiguationData":[TD([[makeQuery(id+"F17.imprint","IMPRINT",EDGE,{"derivedFrom":subQ0}),1.0]])]});}
            var Q2;
            {var subQ0=sQuery(id+"F17.wireOp",EDGE,"E91");var subQ1=makeQuery(id+"F17.imprint","INTERSECT",VERTEX,{"derivedFrom":[sQuery(id+"F17.wireOp",EDGE,"E85.0"),subQ0]});Q2=makeQuery(id+"F17.imprint","IMPRINT",FACE,{"disambiguationData":[TD([[makeQuery(id+"F17.imprint","IMPRINT",EDGE,{"disambiguationData":[TD([[subQ1,1.0]])],"derivedFrom":subQ0}),1.0]])]});}
            var Q3;
            {var subQ0=sQuery(id+"F17.wireOp",EDGE,"E108");var subQ1=sQuery(id+"F17.wireOp",EDGE,"E77");var subQ2=makeQuery(id+"F17.imprint","INTERSECT",VERTEX,{"disambiguationData":[OD(0.0)],"derivedFrom":[subQ1,subQ0]});Q3=makeQuery(id+"F17.imprint","IMPRINT",FACE,{"disambiguationData":[TD([[makeQuery(id+"F17.imprint","IMPRINT",EDGE,{"disambiguationData":[TD([[subQ2,-1.0]])],"derivedFrom":subQ1}),-1.0]])]});}
            var Q4;
            {var subQ0=sQuery(id+"F17.wireOp",EDGE,"E86");var subQ1=sQuery(id+"F17.wireOp",EDGE,"E80.MirrorCS");var subQ2=makeQuery(id+"F17.imprint","INTERSECT",VERTEX,{"derivedFrom":[subQ1,subQ0]});Q4=makeQuery(id+"F17.imprint","IMPRINT",FACE,{"disambiguationData":[TD([[makeQuery(id+"F17.imprint","IMPRINT",EDGE,{"disambiguationData":[TD([[subQ2,-1.0]])],"derivedFrom":subQ1}),1.0]])]});}
            var Q5;
            {var subQ0=sQuery(id+"F17.wireOp",EDGE,"E92");var subQ1=makeQuery(id+"F17.imprint","INTERSECT",VERTEX,{"derivedFrom":[sQuery(id+"F17.wireOp",EDGE,"E65"),subQ0]});Q5=makeQuery(id+"F17.imprint","IMPRINT",FACE,{"disambiguationData":[TD([[makeQuery(id+"F17.imprint","IMPRINT",EDGE,{"disambiguationData":[TD([[subQ1,1.0]])],"derivedFrom":subQ0}),1.0]])]});}
            var Q6;
            {var subQ0=sQuery(id+"F17.wireOp",EDGE,"E65");var subQ1=sQuery(id+"F17.wireOp",EDGE,"E64.right");var subQ2=makeQuery(id+"F17.imprint","INTERSECT",VERTEX,{"derivedFrom":[subQ1,subQ0]});Q6=makeQuery(id+"F17.imprint","IMPRINT",FACE,{"disambiguationData":[TD([[makeQuery(id+"F17.imprint","IMPRINT",EDGE,{"disambiguationData":[TD([[subQ2,1.0]])],"derivedFrom":subQ1}),1.0]])]});}
            var Q7;
            {var subQ0=sQuery(id+"F17.wireOp",EDGE,"E67.0");var subQ1=sQuery(id+"F17.wireOp",EDGE,"E64.right");var subQ2=makeQuery(id+"F17.imprint","INTERSECT",VERTEX,{"derivedFrom":[subQ1,subQ0]});Q7=makeQuery(id+"F17.imprint","IMPRINT",FACE,{"disambiguationData":[TD([[makeQuery(id+"F17.imprint","IMPRINT",EDGE,{"disambiguationData":[TD([[subQ2,-1.0]])],"derivedFrom":subQ1}),1.0]])]});}
            var Q8;
            {var subQ0=sQuery(id+"F17.wireOp",EDGE,"E93");var subQ1=makeQuery(id+"F17.imprint","INTERSECT",VERTEX,{"derivedFrom":[sQuery(id+"F17.wireOp",EDGE,"E67.0"),subQ0]});Q8=makeQuery(id+"F17.imprint","IMPRINT",FACE,{"disambiguationData":[TD([[makeQuery(id+"F17.imprint","IMPRINT",EDGE,{"disambiguationData":[TD([[subQ1,-1.0]])],"derivedFrom":subQ0}),1.0]])]});}
            var Q9;
            {var subQ0=sQuery(id+"F17.wireOp",EDGE,"E94");var subQ1=makeQuery(id+"F17.imprint","INTERSECT",VERTEX,{"derivedFrom":[sQuery(id+"F17.wireOp",EDGE,"E69"),subQ0]});Q9=makeQuery(id+"F17.imprint","IMPRINT",FACE,{"disambiguationData":[TD([[makeQuery(id+"F17.imprint","IMPRINT",EDGE,{"disambiguationData":[TD([[subQ1,1.0]])],"derivedFrom":subQ0}),1.0]])]});}
            var Q10;
            {var subQ0=sQuery(id+"F17.wireOp",EDGE,"E69");var subQ5=sQuery(id+"F17.wireOp",EDGE,"E64.right");var subQ8=makeQuery(id+"F17.imprint","INTERSECT",VERTEX,{"derivedFrom":[subQ5,subQ0]});Q10=makeQuery(id+"F17.imprint","IMPRINT",FACE,{"disambiguationData":[TD([[makeQuery(id+"F17.imprint","IMPRINT",EDGE,{"disambiguationData":[TD([[subQ8,1.0]])],"derivedFrom":subQ5}),1.0]])]});}
            var Q11;
            {var subQ1=sQuery(id+"F17.wireOp",EDGE,"E64.right");var subQ6=sQuery(id+"F17.wireOp",EDGE,"E69");var subQ9=makeQuery(id+"F17.imprint","INTERSECT",VERTEX,{"derivedFrom":[subQ1,subQ6]});Q11=makeQuery(id+"F17.imprint","IMPRINT",FACE,{"disambiguationData":[TD([[makeQuery(id+"F17.imprint","IMPRINT",EDGE,{"disambiguationData":[TD([[subQ9,-1.0]])],"derivedFrom":subQ1}),1.0]])]});}
            var Q12;
            {var subQ0=sQuery(id+"F17.wireOp",EDGE,"E100");var subQ1=makeQuery(id+"F17.imprint","INTERSECT",VERTEX,{"derivedFrom":[sQuery(id+"F17.wireOp",EDGE,"E98"),subQ0]});Q12=makeQuery(id+"F17.imprint","IMPRINT",FACE,{"disambiguationData":[TD([[makeQuery(id+"F17.imprint","IMPRINT",EDGE,{"disambiguationData":[TD([[subQ1,1.0]])],"derivedFrom":subQ0}),1.0]])]});}
            var Q13;
            {var subQ0=sQuery(id+"F17.wireOp",EDGE,"E101");var subQ1=sQuery(id+"F17.wireOp",EDGE,"E70.0");var subQ2=makeQuery(id+"F17.imprint","INTERSECT",VERTEX,{"disambiguationData":[OD(0.0)],"derivedFrom":[subQ1,subQ0]});Q13=makeQuery(id+"F17.imprint","IMPRINT",FACE,{"disambiguationData":[TD([[makeQuery(id+"F17.imprint","IMPRINT",EDGE,{"disambiguationData":[TD([[subQ2,-1.0]])],"derivedFrom":subQ1}),-1.0]])]});}
            var Q14;
            {var subQ0=sQuery(id+"F17.wireOp",EDGE,"E68");var subQ7=sQuery(id+"F17.wireOp",EDGE,"E64.left");var subQ8=makeQuery(id+"F17.imprint","INTERSECT",VERTEX,{"derivedFrom":[subQ7,subQ0]});Q14=makeQuery(id+"F17.imprint","IMPRINT",FACE,{"disambiguationData":[TD([[makeQuery(id+"F17.imprint","IMPRINT",EDGE,{"disambiguationData":[TD([[subQ8,1.0]])],"derivedFrom":subQ7}),-1.0]])]});}
            var Q15;
            {var subQ0=sQuery(id+"F17.wireOp",EDGE,"E171");var subQ1=makeQuery(id+"F17.imprint","INTERSECT",VERTEX,{"derivedFrom":[sQuery(id+"F17.wireOp",EDGE,"E68"),subQ0]});Q15=makeQuery(id+"F17.imprint","IMPRINT",FACE,{"disambiguationData":[TD([[makeQuery(id+"F17.imprint","IMPRINT",EDGE,{"disambiguationData":[TD([[subQ1,-1.0]])],"derivedFrom":subQ0}),1.0]])]});}
            var Q16;
            {var subQ0=sQuery(id+"F17.wireOp",EDGE,"E97");var subQ1=makeQuery(id+"F17.imprint","INTERSECT",VERTEX,{"derivedFrom":[sQuery(id+"F17.wireOp",EDGE,"E95"),subQ0]});Q16=makeQuery(id+"F17.imprint","IMPRINT",FACE,{"disambiguationData":[TD([[makeQuery(id+"F17.imprint","IMPRINT",EDGE,{"disambiguationData":[TD([[subQ1,1.0]])],"derivedFrom":subQ0}),1.0]])]});}
            var Q17;
            {var subQ0=sQuery(id+"F17.wireOp",EDGE,"E95");var subQ1=sQuery(id+"F17.wireOp",EDGE,"E68");var subQ2=makeQuery(id+"F17.imprint","INTERSECT",VERTEX,{"derivedFrom":[subQ1,subQ0]});Q17=makeQuery(id+"F17.imprint","IMPRINT",FACE,{"disambiguationData":[TD([[makeQuery(id+"F17.imprint","IMPRINT",EDGE,{"disambiguationData":[TD([[subQ2,-1.0]])],"derivedFrom":subQ1}),1.0]])]});}
            var Q18;
            {var subQ0=sQuery(id+"F17.wireOp",EDGE,"E101");var subQ1=sQuery(id+"F17.wireOp",EDGE,"E70.0");var subQ2=makeQuery(id+"F17.imprint","INTERSECT",VERTEX,{"disambiguationData":[OD(0.0)],"derivedFrom":[subQ1,subQ0]});Q18=makeQuery(id+"F17.imprint","IMPRINT",FACE,{"disambiguationData":[TD([[makeQuery(id+"F17.imprint","IMPRINT",EDGE,{"disambiguationData":[TD([[subQ2,-1.0]])],"derivedFrom":subQ1}),1.0]])]});}
            var Q19;
            {var subQ2=sQuery(id+"F17.wireOp",EDGE,"E103");Q19=makeQuery(id+"F17.imprint","IMPRINT",FACE,{"disambiguationData":[TD([[makeQuery(id+"F17.imprint","IMPRINT",EDGE,{"derivedFrom":subQ2}),-1.0]])]});}
            var Q20;
            {var subQ0=sQuery(id+"F17.wireOp",EDGE,"E102");Q20=makeQuery(id+"F17.imprint","IMPRINT",FACE,{"disambiguationData":[TD([[makeQuery(id+"F17.imprint","IMPRINT",EDGE,{"derivedFrom":subQ0}),1.0]])]});}
            var Q21;
            Q21=makeQuery(id+"F17.imprint","IMPRINT",FACE,{"disambiguationData":[TD([[makeQuery(id+"F17.imprint","IMPRINT",EDGE,{"derivedFrom":sQuery(id+"F17.wireOp",EDGE,"E140.MirrorCS")}),-1.0]])]});
            var Q22;
            {var subQ0=sQuery(id+"F17.wireOp",EDGE,"E150.MirrorC");var subQ1=makeQuery(id+"F17.imprint","INTERSECT",VERTEX,{"derivedFrom":[sQuery(id+"F17.wireOp",EDGE,"E149.MirrorCS"),subQ0]});Q22=makeQuery(id+"F17.imprint","IMPRINT",FACE,{"disambiguationData":[TD([[makeQuery(id+"F17.imprint","IMPRINT",EDGE,{"disambiguationData":[TD([[subQ1,-1.0]])],"derivedFrom":subQ0}),-1.0]])]});}
            var Q23;
            {var subQ0=sQuery(id+"F17.wireOp",EDGE,"E147.MirrorC");var subQ1=makeQuery(id+"F17.imprint","INTERSECT",VERTEX,{"derivedFrom":[sQuery(id+"F17.wireOp",EDGE,"E139.MirrorCS"),subQ0]});Q23=makeQuery(id+"F17.imprint","IMPRINT",FACE,{"disambiguationData":[TD([[makeQuery(id+"F17.imprint","IMPRINT",EDGE,{"disambiguationData":[TD([[subQ1,1.0]])],"derivedFrom":subQ0}),-1.0]])]});}
            var Q24;
            {var subQ5=sQuery(id+"F17.wireOp",EDGE,"E139.MirrorCS");var subQ7=sQuery(id+"F17.wireOp",EDGE,"E146.MirrorCS");var subQ8=makeQuery(id+"F17.imprint","INTERSECT",VERTEX,{"derivedFrom":[subQ5,subQ7]});Q24=makeQuery(id+"F17.imprint","IMPRINT",FACE,{"disambiguationData":[TD([[makeQuery(id+"F17.imprint","IMPRINT",EDGE,{"disambiguationData":[TD([[subQ8,-1.0]])],"derivedFrom":subQ5}),1.0]])]});}
            var Q25;
            {var subQ0=sQuery(id+"F17.wireOp",EDGE,"E145.MirrorC");var subQ1=makeQuery(id+"F17.imprint","INTERSECT",VERTEX,{"derivedFrom":[sQuery(id+"F17.wireOp",EDGE,"E144.MirrorCS"),subQ0]});Q25=makeQuery(id+"F17.imprint","IMPRINT",FACE,{"disambiguationData":[TD([[makeQuery(id+"F17.imprint","IMPRINT",EDGE,{"disambiguationData":[TD([[subQ1,-1.0]])],"derivedFrom":subQ0}),-1.0]])]});}
            var Q26;
            {var subQ1=sQuery(id+"F17.wireOp",EDGE,"E137.MirrorCS");var subQ5=sQuery(id+"F17.wireOp",EDGE,"E139.MirrorCS");var subQ6=makeQuery(id+"F17.imprint","INTERSECT",VERTEX,{"derivedFrom":[subQ1,subQ5]});Q26=makeQuery(id+"F17.imprint","IMPRINT",FACE,{"disambiguationData":[TD([[makeQuery(id+"F17.imprint","IMPRINT",EDGE,{"disambiguationData":[TD([[subQ6,-1.0]])],"derivedFrom":subQ1}),-1.0]])]});}
            var Q27;
            {var subQ0=sQuery(id+"F17.wireOp",EDGE,"E169");var subQ1=makeQuery(id+"F17.imprint","INTERSECT",VERTEX,{"derivedFrom":[sQuery(id+"F17.wireOp",EDGE,"E137.MirrorCS"),subQ0]});Q27=makeQuery(id+"F17.imprint","IMPRINT",FACE,{"disambiguationData":[TD([[makeQuery(id+"F17.imprint","IMPRINT",EDGE,{"disambiguationData":[TD([[subQ1,-1.0]])],"derivedFrom":subQ0}),1.0]])]});}
            var Q28;
            {var subQ0=sQuery(id+"F17.wireOp",EDGE,"E138.MirrorC");var subQ1=sQuery(id+"F17.wireOp",EDGE,"E137.MirrorCS");var subQ2=makeQuery(id+"F17.imprint","INTERSECT",VERTEX,{"disambiguationData":[OD(0.0)],"derivedFrom":[subQ1,subQ0]});Q28=makeQuery(id+"F17.imprint","IMPRINT",FACE,{"disambiguationData":[TD([[makeQuery(id+"F17.imprint","IMPRINT",EDGE,{"disambiguationData":[TD([[subQ2,-1.0]])],"derivedFrom":subQ1}),1.0]])]});}
            var Q29;
            {var subQ0=sQuery(id+"F17.wireOp",EDGE,"E135.MirrorCS");var subQ1=sQuery(id+"F17.wireOp",EDGE,"E134.MirrorC");var subQ2=makeQuery(id+"F17.imprint","INTERSECT",VERTEX,{"derivedFrom":[subQ1,subQ0]});Q29=makeQuery(id+"F17.imprint","IMPRINT",FACE,{"disambiguationData":[TD([[makeQuery(id+"F17.imprint","IMPRINT",EDGE,{"disambiguationData":[TD([[subQ2,-1.0]])],"derivedFrom":subQ1}),1.0]])]});}
            var Q30;
            {var subQ0=sQuery(id+"F17.wireOp",EDGE,"E134.MirrorC");var subQ1=makeQuery(id+"F17.imprint","INTERSECT",VERTEX,{"derivedFrom":[subQ0,sQuery(id+"F17.wireOp",EDGE,"E135.MirrorCS")]});Q30=makeQuery(id+"F17.imprint","IMPRINT",FACE,{"disambiguationData":[TD([[makeQuery(id+"F17.imprint","IMPRINT",EDGE,{"disambiguationData":[TD([[subQ1,1.0]])],"derivedFrom":subQ0}),-1.0]])]});}
            var Q31;
            {var subQ0=sQuery(id+"F17.wireOp",EDGE,"E138.MirrorC");var subQ1=sQuery(id+"F17.wireOp",EDGE,"E137.MirrorCS");var subQ2=makeQuery(id+"F17.imprint","INTERSECT",VERTEX,{"disambiguationData":[OD(0.0)],"derivedFrom":[subQ1,subQ0]});Q31=makeQuery(id+"F17.imprint","IMPRINT",FACE,{"disambiguationData":[TD([[makeQuery(id+"F17.imprint","IMPRINT",EDGE,{"disambiguationData":[TD([[subQ2,-1.0]])],"derivedFrom":subQ1}),-1.0]])]});}
            var Q32;
            {var subQ0=sQuery(id+"F17.wireOp",EDGE,"E162.MirrorCS");var subQ1=sQuery(id+"F17.wireOp",EDGE,"E151.MirrorCS");var subQ2=makeQuery(id+"F17.imprint","INTERSECT",VERTEX,{"derivedFrom":[subQ1,subQ0]});Q32=makeQuery(id+"F17.imprint","IMPRINT",FACE,{"disambiguationData":[TD([[makeQuery(id+"F17.imprint","IMPRINT",EDGE,{"disambiguationData":[TD([[subQ2,1.0]])],"derivedFrom":subQ1}),-1.0]])]});}
            var Q33;
            {var subQ0=sQuery(id+"F17.wireOp",EDGE,"E159.MirrorCS");var subQ1=sQuery(id+"F17.wireOp",EDGE,"E151.MirrorCS");var subQ2=makeQuery(id+"F17.imprint","INTERSECT",VERTEX,{"derivedFrom":[subQ1,subQ0]});Q33=makeQuery(id+"F17.imprint","IMPRINT",FACE,{"disambiguationData":[TD([[makeQuery(id+"F17.imprint","IMPRINT",EDGE,{"disambiguationData":[TD([[subQ2,-1.0]])],"derivedFrom":subQ1}),-1.0]])]});}
            var Q34;
            {var subQ0=sQuery(id+"F17.wireOp",EDGE,"E158.MirrorC");var subQ1=makeQuery(id+"F17.imprint","INTERSECT",VERTEX,{"derivedFrom":[subQ0,sQuery(id+"F17.wireOp",EDGE,"E159.MirrorCS")]});Q34=makeQuery(id+"F17.imprint","IMPRINT",FACE,{"disambiguationData":[TD([[makeQuery(id+"F17.imprint","IMPRINT",EDGE,{"disambiguationData":[TD([[subQ1,-1.0]])],"derivedFrom":subQ0}),-1.0]])]});}
            var Q35;
            {var subQ0=sQuery(id+"F17.wireOp",EDGE,"E163.MirrorC");var subQ1=sQuery(id+"F17.wireOp",EDGE,"E162.MirrorCS");var subQ2=makeQuery(id+"F17.imprint","INTERSECT",VERTEX,{"disambiguationData":[OD(0.0)],"derivedFrom":[subQ1,subQ0]});Q35=makeQuery(id+"F17.imprint","IMPRINT",FACE,{"disambiguationData":[TD([[makeQuery(id+"F17.imprint","IMPRINT",EDGE,{"disambiguationData":[TD([[subQ2,1.0]])],"derivedFrom":subQ1}),-1.0]])]});}
            var Q36;
            {var subQ3=sQuery(id+"F17.wireOp",EDGE,"E153.MirrorCS");var subQ5=sQuery(id+"F17.wireOp",EDGE,"E151.MirrorCS");var subQ6=makeQuery(id+"F17.imprint","INTERSECT",VERTEX,{"derivedFrom":[subQ5,subQ3]});Q36=makeQuery(id+"F17.imprint","IMPRINT",FACE,{"disambiguationData":[TD([[makeQuery(id+"F17.imprint","IMPRINT",EDGE,{"disambiguationData":[TD([[subQ6,-1.0]])],"derivedFrom":subQ5}),-1.0]])]});}
            var Q37;
            {var subQ0=sQuery(id+"F17.wireOp",EDGE,"E157.MirrorC");var subQ1=makeQuery(id+"F17.imprint","INTERSECT",VERTEX,{"derivedFrom":[sQuery(id+"F17.wireOp",EDGE,"E155.MirrorCS"),subQ0]});Q37=makeQuery(id+"F17.imprint","IMPRINT",FACE,{"disambiguationData":[TD([[makeQuery(id+"F17.imprint","IMPRINT",EDGE,{"disambiguationData":[TD([[subQ1,-1.0]])],"derivedFrom":subQ0}),-1.0]])]});}
            var Q38;
            {var subQ1=sQuery(id+"F17.wireOp",EDGE,"E152.MirrorCS");var subQ5=sQuery(id+"F17.wireOp",EDGE,"E151.MirrorCS");var subQ6=makeQuery(id+"F17.imprint","INTERSECT",VERTEX,{"derivedFrom":[subQ5,subQ1]});Q38=makeQuery(id+"F17.imprint","IMPRINT",FACE,{"disambiguationData":[TD([[makeQuery(id+"F17.imprint","IMPRINT",EDGE,{"disambiguationData":[TD([[subQ6,-1.0]])],"derivedFrom":subQ5}),-1.0]])]});}
            var Q39;
            {var subQ0=sQuery(id+"F17.wireOp",EDGE,"E154.MirrorC");var subQ1=makeQuery(id+"F17.imprint","INTERSECT",VERTEX,{"derivedFrom":[sQuery(id+"F17.wireOp",EDGE,"E152.MirrorCS"),subQ0]});Q39=makeQuery(id+"F17.imprint","IMPRINT",FACE,{"disambiguationData":[TD([[makeQuery(id+"F17.imprint","IMPRINT",EDGE,{"disambiguationData":[TD([[subQ1,-1.0]])],"derivedFrom":subQ0}),-1.0]])]});}
            var Q40;
            {var subQ0=sQuery(id+"F17.wireOp",EDGE,"E155.MirrorCS");var subQ1=sQuery(id+"F17.wireOp",EDGE,"E151.MirrorCS");var subQ2=makeQuery(id+"F17.imprint","INTERSECT",VERTEX,{"derivedFrom":[subQ1,subQ0]});Q40=makeQuery(id+"F17.imprint","IMPRINT",FACE,{"disambiguationData":[TD([[makeQuery(id+"F17.imprint","IMPRINT",EDGE,{"disambiguationData":[TD([[subQ2,-1.0]])],"derivedFrom":subQ1}),-1.0]])]});}
            var Q41;
            Q41=makeQuery(id+"F17.imprint","IMPRINT",FACE,{"disambiguationData":[TD([[makeQuery(id+"F17.imprint","IMPRINT",EDGE,{"derivedFrom":sQuery(id+"F17.wireOp",EDGE,"E119")}),-1.0]])]});
            var Q42;
            Q42=makeQuery(id+"F17.imprint","IMPRINT",FACE,{"disambiguationData":[TD([[makeQuery(id+"F17.imprint","IMPRINT",EDGE,{"derivedFrom":sQuery(id+"F17.wireOp",EDGE,"E110.MirrorCS")}),1.0]])]});
            extrude(context, id + "F18", {"entities" : qUnion([Q0, Q1, Q2, Q3, Q4, Q5, Q6, Q7, Q8, Q9, Q10, Q11, Q12, Q13, Q14, Q15, Q16, Q17, Q18, Q19, Q20, Q21, Q22, Q23, Q24, Q25, Q26, Q27, Q28, Q29, Q30, Q31, Q32, Q33, Q34, Q35, Q36, Q37, Q38, Q39, Q40, Q41, Q42]), "oppositeDirection" : true, "depth" : 20 * mm});
        }
        {
            var Q0;
            Q0=makeQuery(id+"F1.opExtrude","CAP_FACE",FACE,{"disambiguationData":[OSD([sQuery(id+"F0.wireOp",EDGE,"E0.bottom"),sQuery(id+"F0.wireOp",EDGE,"E0.top"),sQuery(id+"F0.wireOp",EDGE,"E0.left"),sQuery(id+"F0.wireOp",EDGE,"E0.right"),sQuery(id+"F0.wireOp",EDGE,"E1.rect.bottom"),sQuery(id+"F0.wireOp",EDGE,"E1.rect.left"),sQuery(id+"F0.wireOp",EDGE,"E1.rect.right"),sQuery(id+"F0.wireOp",EDGE,"E2.rect.bottom"),sQuery(id+"F0.wireOp",EDGE,"E2.rect.top"),sQuery(id+"F0.wireOp",EDGE,"E2.rect.right"),sQuery(id+"F0.wireOp",EDGE,"E3.rect.top"),sQuery(id+"F0.wireOp",EDGE,"E3.rect.left"),sQuery(id+"F0.wireOp",EDGE,"E3.rect.right"),sQuery(id+"F0.wireOp",EDGE,"E4.rect.bottom"),sQuery(id+"F0.wireOp",EDGE,"E4.rect.top"),sQuery(id+"F0.wireOp",EDGE,"E4.rect.left")])],"isStart":true});
            var sketch = newSketch(context, id + "F19", { "sketchPlane" : qUnion([Q0])});
            skLineSegment(sketch, "E172.rect.bottom", {"start": v(449.97, -113.3) * mm, "end": v(399.97, -113.3) * mm});
            skLineSegment(sketch, "E172.rect.top", {"start": v(449.97, -93.3) * mm, "end": v(399.97, -93.3) * mm});
            skLineSegment(sketch, "E172.rect.left", {"start": v(449.97, -113.3) * mm, "end": v(449.97, -93.3) * mm});
            skLineSegment(sketch, "E172.rect.right", {"start": v(399.97, -113.3) * mm, "end": v(399.97, -93.3) * mm});
            skPoint(sketch, "E172.rect.middle", {"position": v(424.97, -103.3) * mm});
            skPoint(sketch, "E172.rect.middle.positionSnap0", {"position": v(229.97, -103.3) * mm});
            skPoint(sketch, "E172.rect.middle.positionSnap1", {"position": v(424.97, 77.01) * mm});
            skPoint(sketch, "E172.rect.centerSnap0", {"position": v(229.97, -103.3) * mm});
            skPoint(sketch, "E172.rect.centerSnap1", {"position": v(424.97, 77.01) * mm});
            skLineSegment(sketch, "E173.rect.bottom", {"start": v(434.97, -128.3) * mm, "end": v(414.97, -128.3) * mm});
            skLineSegment(sketch, "E173.rect.top", {"start": v(434.97, -78.3) * mm, "end": v(414.97, -78.3) * mm});
            skLineSegment(sketch, "E173.rect.left", {"start": v(434.97, -128.3) * mm, "end": v(434.97, -78.3) * mm});
            skLineSegment(sketch, "E173.rect.right", {"start": v(414.97, -128.3) * mm, "end": v(414.97, -78.3) * mm});
            skSolve(sketch);
        }
        {
            var Q0;
            {var subQ0=sQuery(id+"F19.wireOp",EDGE,"E172.rect.left");Q0=makeQuery(id+"F19.imprint","IMPRINT",FACE,{"disambiguationData":[TD([[makeQuery(id+"F19.imprint","IMPRINT",EDGE,{"derivedFrom":subQ0}),1.0]])]});}
            var Q1;
            {var subQ0=sQuery(id+"F19.wireOp",EDGE,"E172.rect.right");Q1=makeQuery(id+"F19.imprint","IMPRINT",FACE,{"disambiguationData":[TD([[makeQuery(id+"F19.imprint","IMPRINT",EDGE,{"derivedFrom":subQ0}),-1.0]])]});}
            var Q2;
            {var subQ0=sQuery(id+"F19.wireOp",EDGE,"E173.rect.left");var subQ1=sQuery(id+"F19.wireOp",EDGE,"E172.rect.bottom");var subQ2=makeQuery(id+"F19.imprint","INTERSECT",VERTEX,{"derivedFrom":[subQ1,subQ0]});Q2=makeQuery(id+"F19.imprint","IMPRINT",FACE,{"disambiguationData":[TD([[makeQuery(id+"F19.imprint","IMPRINT",EDGE,{"disambiguationData":[TD([[subQ2,-1.0]])],"derivedFrom":subQ1}),-1.0]])]});}
            var Q3;
            Q3=makeQuery(id+"F10.opExtrude","CAP_FACE",FACE,{"disambiguationData":[OSD([sQuery(id+"F9.wireOp",EDGE,"E48.bottom"),sQuery(id+"F9.wireOp",EDGE,"E48.top"),sQuery(id+"F9.wireOp",EDGE,"E48.left"),sQuery(id+"F9.wireOp",EDGE,"E48.right"),sQuery(id+"F9.wireOp",EDGE,"E49.top"),sQuery(id+"F9.wireOp",EDGE,"E49.left"),sQuery(id+"F9.wireOp",EDGE,"E49.right"),sQuery(id+"F9.wireOp",EDGE,"E50.top"),sQuery(id+"F9.wireOp",EDGE,"E50.left"),sQuery(id+"F9.wireOp",EDGE,"E50.right"),sQuery(id+"F9.wireOp",EDGE,"E51.top"),sQuery(id+"F9.wireOp",EDGE,"E51.left"),sQuery(id+"F9.wireOp",EDGE,"E51.right"),sQuery(id+"F9.wireOp",EDGE,"E53.MirrorCS"),sQuery(id+"F9.wireOp",EDGE,"E54.MirrorCS"),sQuery(id+"F9.wireOp",EDGE,"E55.MirrorCS")])],"isStart":false});
            extrude(context, id + "F20", {"entities" : qUnion([Q0, Q1, Q2]), "operationType" : NewBodyOperationType.REMOVE, "endBound" : BoundingType.UP_TO_SURFACE, "oppositeDirection" : true, "endBoundEntityFace" : qUnion([Q3]), "depth" : 25 * mm});
        }
        {
            var Q0;
            {var subQ5=sQuery(id+"F19.wireOp",EDGE,"E173.rect.bottom");Q0=makeQuery(id+"F19.imprint","IMPRINT",FACE,{"disambiguationData":[TD([[makeQuery(id+"F19.imprint","IMPRINT",EDGE,{"derivedFrom":subQ5}),-1.0]])]});}
            var Q1;
            {var subQ5=sQuery(id+"F19.wireOp",EDGE,"E173.rect.top");Q1=makeQuery(id+"F19.imprint","IMPRINT",FACE,{"disambiguationData":[TD([[makeQuery(id+"F19.imprint","IMPRINT",EDGE,{"derivedFrom":subQ5}),1.0]])]});}
            var Q2;
            {var subQ0=sQuery(id+"F19.wireOp",EDGE,"E173.rect.left");var subQ1=sQuery(id+"F19.wireOp",EDGE,"E172.rect.bottom");var subQ2=makeQuery(id+"F19.imprint","INTERSECT",VERTEX,{"derivedFrom":[subQ1,subQ0]});Q2=makeQuery(id+"F19.imprint","IMPRINT",FACE,{"disambiguationData":[TD([[makeQuery(id+"F19.imprint","IMPRINT",EDGE,{"disambiguationData":[TD([[subQ2,-1.0]])],"derivedFrom":subQ1}),-1.0]])]});}
            var Q3;
            Q3=makeQuery(id+"F10.opExtrude","CAP_FACE",FACE,{"disambiguationData":[OSD([sQuery(id+"F9.wireOp",EDGE,"E48.bottom"),sQuery(id+"F9.wireOp",EDGE,"E48.top"),sQuery(id+"F9.wireOp",EDGE,"E48.left"),sQuery(id+"F9.wireOp",EDGE,"E48.right"),sQuery(id+"F9.wireOp",EDGE,"E49.top"),sQuery(id+"F9.wireOp",EDGE,"E49.left"),sQuery(id+"F9.wireOp",EDGE,"E49.right"),sQuery(id+"F9.wireOp",EDGE,"E50.top"),sQuery(id+"F9.wireOp",EDGE,"E50.left"),sQuery(id+"F9.wireOp",EDGE,"E50.right"),sQuery(id+"F9.wireOp",EDGE,"E51.top"),sQuery(id+"F9.wireOp",EDGE,"E51.left"),sQuery(id+"F9.wireOp",EDGE,"E51.right"),sQuery(id+"F9.wireOp",EDGE,"E53.MirrorCS"),sQuery(id+"F9.wireOp",EDGE,"E54.MirrorCS"),sQuery(id+"F9.wireOp",EDGE,"E55.MirrorCS")])],"isStart":false});
            extrude(context, id + "F21", {"entities" : qUnion([Q0, Q1, Q2]), "operationType" : NewBodyOperationType.REMOVE, "endBound" : BoundingType.UP_TO_SURFACE, "oppositeDirection" : true, "endBoundEntityFace" : qUnion([Q3]), "depth" : 25 * mm});
        }
        {
            var Q0;
            Q0=makeQuery(id+"F11.opPattern","COPY",BODY,{"derivedFrom":makeQuery(id+"F10.opExtrude","SWEPT_BODY",BODY,{"disambiguationData":[OSD([sQuery(id+"F9.wireOp",EDGE,"E48.bottom"),sQuery(id+"F9.wireOp",EDGE,"E48.top"),sQuery(id+"F9.wireOp",EDGE,"E48.left"),sQuery(id+"F9.wireOp",EDGE,"E48.right"),sQuery(id+"F9.wireOp",EDGE,"E49.top"),sQuery(id+"F9.wireOp",EDGE,"E49.left"),sQuery(id+"F9.wireOp",EDGE,"E49.right"),sQuery(id+"F9.wireOp",EDGE,"E50.top"),sQuery(id+"F9.wireOp",EDGE,"E50.left"),sQuery(id+"F9.wireOp",EDGE,"E50.right"),sQuery(id+"F9.wireOp",EDGE,"E51.top"),sQuery(id+"F9.wireOp",EDGE,"E51.left"),sQuery(id+"F9.wireOp",EDGE,"E51.right"),sQuery(id+"F9.wireOp",EDGE,"E53.MirrorCS"),sQuery(id+"F9.wireOp",EDGE,"E54.MirrorCS"),sQuery(id+"F9.wireOp",EDGE,"E55.MirrorCS")])]}),"instanceName":"1"});
            var Q1;
            Q1=makeQuery(id+"F10.opExtrude","SWEPT_BODY",BODY,{"disambiguationData":[OSD([sQuery(id+"F9.wireOp",EDGE,"E48.bottom"),sQuery(id+"F9.wireOp",EDGE,"E48.top"),sQuery(id+"F9.wireOp",EDGE,"E48.left"),sQuery(id+"F9.wireOp",EDGE,"E48.right"),sQuery(id+"F9.wireOp",EDGE,"E49.top"),sQuery(id+"F9.wireOp",EDGE,"E49.left"),sQuery(id+"F9.wireOp",EDGE,"E49.right"),sQuery(id+"F9.wireOp",EDGE,"E50.top"),sQuery(id+"F9.wireOp",EDGE,"E50.left"),sQuery(id+"F9.wireOp",EDGE,"E50.right"),sQuery(id+"F9.wireOp",EDGE,"E51.top"),sQuery(id+"F9.wireOp",EDGE,"E51.left"),sQuery(id+"F9.wireOp",EDGE,"E51.right"),sQuery(id+"F9.wireOp",EDGE,"E53.MirrorCS"),sQuery(id+"F9.wireOp",EDGE,"E54.MirrorCS"),sQuery(id+"F9.wireOp",EDGE,"E55.MirrorCS")])]});
            var Q2;
            Q2=makeQuery(id+"F1.opExtrude","SWEPT_BODY",BODY,{"disambiguationData":[OSD([sQuery(id+"F0.wireOp",EDGE,"E0.bottom"),sQuery(id+"F0.wireOp",EDGE,"E0.top"),sQuery(id+"F0.wireOp",EDGE,"E0.left"),sQuery(id+"F0.wireOp",EDGE,"E0.right"),sQuery(id+"F0.wireOp",EDGE,"E1.rect.bottom"),sQuery(id+"F0.wireOp",EDGE,"E1.rect.left"),sQuery(id+"F0.wireOp",EDGE,"E1.rect.right"),sQuery(id+"F0.wireOp",EDGE,"E2.rect.bottom"),sQuery(id+"F0.wireOp",EDGE,"E2.rect.top"),sQuery(id+"F0.wireOp",EDGE,"E2.rect.right"),sQuery(id+"F0.wireOp",EDGE,"E3.rect.top"),sQuery(id+"F0.wireOp",EDGE,"E3.rect.left"),sQuery(id+"F0.wireOp",EDGE,"E3.rect.right"),sQuery(id+"F0.wireOp",EDGE,"E4.rect.bottom"),sQuery(id+"F0.wireOp",EDGE,"E4.rect.top"),sQuery(id+"F0.wireOp",EDGE,"E4.rect.left")])]});
            transform(context, id + "F22", {"entities" : qUnion([Q0, Q1, Q2]), "transformType" : TransformType.TRANSLATION_3D, "dx" : 1800 * mm, "dy" : 0 * mm, "dz" : 0 * mm, "makeCopy" : true});
        }
        {
            var Q0;
            Q0=makeQuery(id+"F22.opPattern","COPY",BODY,{"derivedFrom":makeQuery(id+"F11.opPattern","COPY",BODY,{"derivedFrom":makeQuery(id+"F10.opExtrude","SWEPT_BODY",BODY,{"disambiguationData":[OSD([sQuery(id+"F9.wireOp",EDGE,"E48.bottom"),sQuery(id+"F9.wireOp",EDGE,"E48.top"),sQuery(id+"F9.wireOp",EDGE,"E48.left"),sQuery(id+"F9.wireOp",EDGE,"E48.right"),sQuery(id+"F9.wireOp",EDGE,"E49.top"),sQuery(id+"F9.wireOp",EDGE,"E49.left"),sQuery(id+"F9.wireOp",EDGE,"E49.right"),sQuery(id+"F9.wireOp",EDGE,"E50.top"),sQuery(id+"F9.wireOp",EDGE,"E50.left"),sQuery(id+"F9.wireOp",EDGE,"E50.right"),sQuery(id+"F9.wireOp",EDGE,"E51.top"),sQuery(id+"F9.wireOp",EDGE,"E51.left"),sQuery(id+"F9.wireOp",EDGE,"E51.right"),sQuery(id+"F9.wireOp",EDGE,"E53.MirrorCS"),sQuery(id+"F9.wireOp",EDGE,"E54.MirrorCS"),sQuery(id+"F9.wireOp",EDGE,"E55.MirrorCS")])]}),"instanceName":"1"}),"instanceName":"1"});
            var Q1;
            Q1=makeQuery(id+"F22.opPattern","COPY",BODY,{"derivedFrom":makeQuery(id+"F10.opExtrude","SWEPT_BODY",BODY,{"disambiguationData":[OSD([sQuery(id+"F9.wireOp",EDGE,"E48.bottom"),sQuery(id+"F9.wireOp",EDGE,"E48.top"),sQuery(id+"F9.wireOp",EDGE,"E48.left"),sQuery(id+"F9.wireOp",EDGE,"E48.right"),sQuery(id+"F9.wireOp",EDGE,"E49.top"),sQuery(id+"F9.wireOp",EDGE,"E49.left"),sQuery(id+"F9.wireOp",EDGE,"E49.right"),sQuery(id+"F9.wireOp",EDGE,"E50.top"),sQuery(id+"F9.wireOp",EDGE,"E50.left"),sQuery(id+"F9.wireOp",EDGE,"E50.right"),sQuery(id+"F9.wireOp",EDGE,"E51.top"),sQuery(id+"F9.wireOp",EDGE,"E51.left"),sQuery(id+"F9.wireOp",EDGE,"E51.right"),sQuery(id+"F9.wireOp",EDGE,"E53.MirrorCS"),sQuery(id+"F9.wireOp",EDGE,"E54.MirrorCS"),sQuery(id+"F9.wireOp",EDGE,"E55.MirrorCS")])]}),"instanceName":"1"});
            var Q2;
            Q2=makeQuery(id+"F22.opPattern","COPY",BODY,{"derivedFrom":makeQuery(id+"F1.opExtrude","SWEPT_BODY",BODY,{"disambiguationData":[OSD([sQuery(id+"F0.wireOp",EDGE,"E0.bottom"),sQuery(id+"F0.wireOp",EDGE,"E0.top"),sQuery(id+"F0.wireOp",EDGE,"E0.left"),sQuery(id+"F0.wireOp",EDGE,"E0.right"),sQuery(id+"F0.wireOp",EDGE,"E1.rect.bottom"),sQuery(id+"F0.wireOp",EDGE,"E1.rect.left"),sQuery(id+"F0.wireOp",EDGE,"E1.rect.right"),sQuery(id+"F0.wireOp",EDGE,"E2.rect.bottom"),sQuery(id+"F0.wireOp",EDGE,"E2.rect.top"),sQuery(id+"F0.wireOp",EDGE,"E2.rect.right"),sQuery(id+"F0.wireOp",EDGE,"E3.rect.top"),sQuery(id+"F0.wireOp",EDGE,"E3.rect.left"),sQuery(id+"F0.wireOp",EDGE,"E3.rect.right"),sQuery(id+"F0.wireOp",EDGE,"E4.rect.bottom"),sQuery(id+"F0.wireOp",EDGE,"E4.rect.top"),sQuery(id+"F0.wireOp",EDGE,"E4.rect.left")])]}),"instanceName":"1"});
            var Q3;
            Q3=makeQuery(id+"F22.opPattern","COPY",EDGE,{"derivedFrom":makeQuery(id+"F10.opExtrude","CAP_EDGE",EDGE,{"disambiguationData":[OSD([sQuery(id+"F9.wireOp",EDGE,"E53.MirrorCS")])],"isStart":false}),"instanceName":"1"});
            transform(context, id + "F23", {"entities" : qUnion([Q0, Q1, Q2]), "transformType" : TransformType.ROTATION, "transformAxis" : qUnion([Q3]), "angle" : 90 * degree, "makeCopy" : false});
        }
        {
            var Q0;
            Q0=makeQuery(id+"F3.opExtrude","SWEPT_BODY",BODY,{"disambiguationData":[OSD([sQuery(id+"F2.wireOp",EDGE,"E5.bottom"),sQuery(id+"F2.wireOp",EDGE,"E5.top"),sQuery(id+"F2.wireOp",EDGE,"E5.left"),sQuery(id+"F2.wireOp",EDGE,"E5.right"),sQuery(id+"F2.wireOp",EDGE,"E6.rect.top"),sQuery(id+"F2.wireOp",EDGE,"E13"),sQuery(id+"F2.wireOp",EDGE,"E14"),sQuery(id+"F2.wireOp",EDGE,"E15"),sQuery(id+"F2.wireOp",EDGE,"E16"),sQuery(id+"F2.wireOp",EDGE,"E18"),sQuery(id+"F2.wireOp",EDGE,"E19"),sQuery(id+"F2.wireOp",EDGE,"E22.MirrorCS"),sQuery(id+"F2.wireOp",EDGE,"E23.MirrorCS"),sQuery(id+"F2.wireOp",EDGE,"E25.MirrorCS"),sQuery(id+"F2.wireOp",EDGE,"E7.rect.top"),sQuery(id+"F2.wireOp",EDGE,"E26"),sQuery(id+"F2.wireOp",EDGE,"E27.0"),sQuery(id+"F2.wireOp",EDGE,"E28.MirrorC"),sQuery(id+"F2.wireOp",EDGE,"E29.MirrorC"),sQuery(id+"F2.wireOp",EDGE,"E30.left"),sQuery(id+"F2.wireOp",EDGE,"E31.MirrorCS")])]});
            transform(context, id + "F24", {"entities" : qUnion([Q0]), "transformType" : TransformType.TRANSLATION_3D, "dx" : 979.64 * mm, "dy" : 0 * mm, "dz" : 0 * mm, "makeCopy" : true});
        }
        {
            var Q0;
            Q0=makeQuery(id+"F22.opPattern","COPY",BODY,{"derivedFrom":makeQuery(id+"F1.opExtrude","SWEPT_BODY",BODY,{"disambiguationData":[OSD([sQuery(id+"F0.wireOp",EDGE,"E0.bottom"),sQuery(id+"F0.wireOp",EDGE,"E0.top"),sQuery(id+"F0.wireOp",EDGE,"E0.left"),sQuery(id+"F0.wireOp",EDGE,"E0.right"),sQuery(id+"F0.wireOp",EDGE,"E1.rect.bottom"),sQuery(id+"F0.wireOp",EDGE,"E1.rect.left"),sQuery(id+"F0.wireOp",EDGE,"E1.rect.right"),sQuery(id+"F0.wireOp",EDGE,"E2.rect.bottom"),sQuery(id+"F0.wireOp",EDGE,"E2.rect.top"),sQuery(id+"F0.wireOp",EDGE,"E2.rect.right"),sQuery(id+"F0.wireOp",EDGE,"E3.rect.top"),sQuery(id+"F0.wireOp",EDGE,"E3.rect.left"),sQuery(id+"F0.wireOp",EDGE,"E3.rect.right"),sQuery(id+"F0.wireOp",EDGE,"E4.rect.bottom"),sQuery(id+"F0.wireOp",EDGE,"E4.rect.top"),sQuery(id+"F0.wireOp",EDGE,"E4.rect.left")])]}),"instanceName":"1"});
            transform(context, id + "F25", {"entities" : qUnion([Q0]), "transformType" : TransformType.TRANSLATION_3D, "dx" : 626.98 * mm, "dy" : 0 * mm, "dz" : 0 * mm, "makeCopy" : false});
        }
        {
            var Q0;
            Q0=makeQuery(id+"F7.opExtrude","SWEPT_BODY",BODY,{"disambiguationData":[OSD([sQuery(id+"F6.wireOp",EDGE,"E32.bottom"),sQuery(id+"F6.wireOp",EDGE,"E33"),sQuery(id+"F6.wireOp",EDGE,"E34"),sQuery(id+"F6.wireOp",EDGE,"E40")])]});
            transform(context, id + "F26", {"entities" : qUnion([Q0]), "transformType" : TransformType.TRANSLATION_3D, "dx" : 2700 * mm, "dy" : 0 * mm, "dz" : 0 * mm, "makeCopy" : true});
        }
        {
            var Q0;
            Q0=makeQuery(id+"F26.opPattern","COPY",BODY,{"derivedFrom":makeQuery(id+"F7.opExtrude","SWEPT_BODY",BODY,{"disambiguationData":[OSD([sQuery(id+"F6.wireOp",EDGE,"E32.bottom"),sQuery(id+"F6.wireOp",EDGE,"E33"),sQuery(id+"F6.wireOp",EDGE,"E34"),sQuery(id+"F6.wireOp",EDGE,"E40")])]}),"instanceName":"1"});
            var Q1;
            {var subQ0=sQuery(id+"F0.wireOp",EDGE,"E0.right");Q1=makeQuery(id+"F22.opPattern","COPY",EDGE,{"derivedFrom":makeQuery(id+"F1.opExtrude","CAP_EDGE",EDGE,{"disambiguationData":[OSD([subQ0]),TDD([makeQuery(id+"F0.imprint","IMPRINT",EDGE,{"disambiguationData":[TD([[makeQuery(id+"F0.imprint","INTERSECT",VERTEX,{"derivedFrom":[sQuery(id+"F0.wireOp",EDGE,"E0.bottom"),subQ0]}),-1.0]])],"derivedFrom":subQ0})])],"isStart":true}),"instanceName":"1"});}
            transform(context, id + "F27", {"entities" : qUnion([Q0]), "transformType" : TransformType.ROTATION, "transformAxis" : qUnion([Q1]), "angle" : 90 * degree, "oppositeDirection" : true, "makeCopy" : false});
        }
    });
